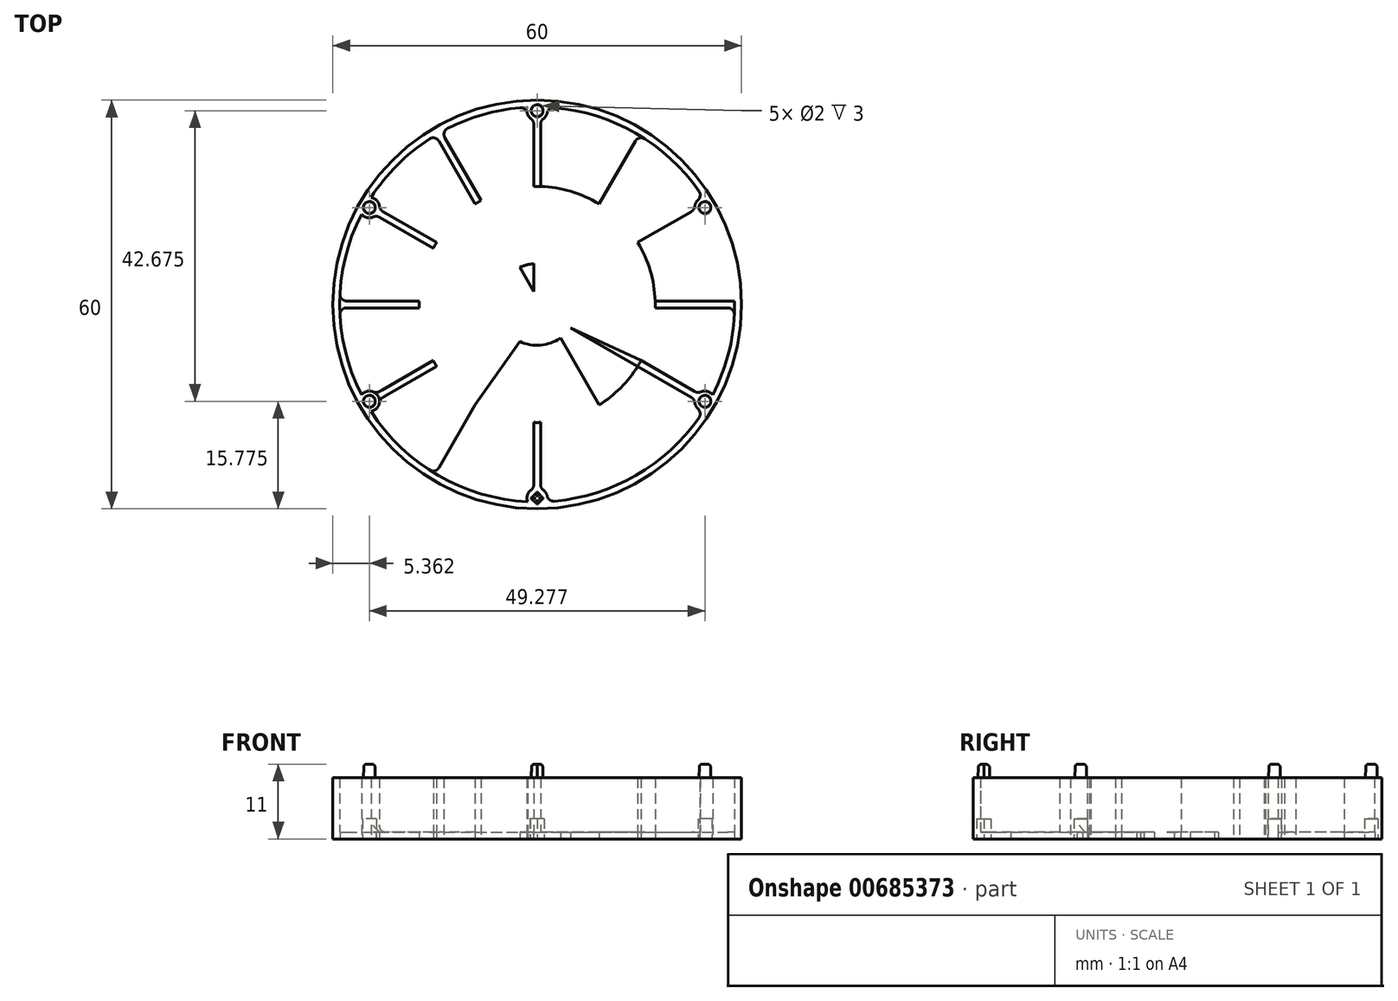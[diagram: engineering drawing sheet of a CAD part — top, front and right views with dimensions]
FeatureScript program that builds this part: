
annotation { "Feature Type Name" : "Feature", "Feature Type Description" : "" }
export const myFeature = defineFeature(function(context is Context, id is Id, definition is map)
    precondition{}
    {
        {
            var Q0;
            Q0=qCreatedBy(makeId("Top.planeOp"),FACE);
            var sketch = newSketch(context, id + "F0", { "sketchPlane" : qUnion([Q0])});
            skCircle(sketch, "E0", {"center": v(0, 0) * mm, "radius": 30 * mm});
            skCircle(sketch, "E1.0", {"center": v(0, 0) * mm, "radius": 29 * mm});
            skLineSegment(sketch, "E2.bottom", {"start": v(14.56, 26.23) * mm, "end": v(15.43, 25.73) * mm});
            skLineSegment(sketch, "E2.top", {"start": v(-15.43, -25.73) * mm, "end": v(-14.56, -26.23) * mm});
            skLineSegment(sketch, "E2.left", {"start": v(14.56, 26.23) * mm, "end": v(-15.43, -25.73) * mm});
            skLineSegment(sketch, "E2.right", {"start": v(15.43, 25.73) * mm, "end": v(-14.56, -26.23) * mm});
            skLineSegment(sketch, "E3.bottom", {"start": v(25.73, 15.43) * mm, "end": v(26.23, 14.56) * mm});
            skLineSegment(sketch, "E3.top", {"start": v(-26.23, -14.56) * mm, "end": v(-25.73, -15.43) * mm});
            skLineSegment(sketch, "E3.left", {"start": v(25.73, 15.43) * mm, "end": v(-26.23, -14.56) * mm});
            skLineSegment(sketch, "E3.right", {"start": v(26.23, 14.56) * mm, "end": v(-25.73, -15.43) * mm});
            skLineSegment(sketch, "E4", {"start": v(-38.35, 0) * mm, "end": v(39.17, 0) * mm, "construction": true});
            skLineSegment(sketch, "E5", {"start": v(0, 42.5) * mm, "end": v(0, -42.47) * mm, "construction": true});
            skLineSegment(sketch, "E6.bottom", {"start": v(-30, 0.5) * mm, "end": v(30, 0.5) * mm});
            skLineSegment(sketch, "E6.top", {"start": v(-30, -0.5) * mm, "end": v(30, -0.5) * mm});
            skLineSegment(sketch, "E6.left", {"start": v(-30, 0.5) * mm, "end": v(-30, -0.5) * mm});
            skLineSegment(sketch, "E6.right", {"start": v(30, 0.5) * mm, "end": v(30, -0.5) * mm});
            skLineSegment(sketch, "E7.bottom", {"start": v(-25.73, 15.43) * mm, "end": v(26.23, -14.56) * mm});
            skLineSegment(sketch, "E7.top", {"start": v(-26.23, 14.56) * mm, "end": v(25.73, -15.43) * mm});
            skLineSegment(sketch, "E7.left", {"start": v(-25.73, 15.43) * mm, "end": v(-26.23, 14.56) * mm});
            skLineSegment(sketch, "E7.right", {"start": v(26.23, -14.56) * mm, "end": v(25.73, -15.43) * mm});
            skLineSegment(sketch, "E8.bottom", {"start": v(-0.5, 30) * mm, "end": v(0.5, 30) * mm});
            skLineSegment(sketch, "E8.top", {"start": v(-0.5, -30) * mm, "end": v(0.5, -30) * mm});
            skLineSegment(sketch, "E8.left", {"start": v(-0.5, 30) * mm, "end": v(-0.5, -30) * mm});
            skLineSegment(sketch, "E8.right", {"start": v(0.5, 30) * mm, "end": v(0.5, -30) * mm});
            skLineSegment(sketch, "E9.bottom", {"start": v(-15.43, 25.73) * mm, "end": v(-14.56, 26.23) * mm});
            skLineSegment(sketch, "E9.top", {"start": v(14.56, -26.23) * mm, "end": v(15.43, -25.73) * mm});
            skLineSegment(sketch, "E9.left", {"start": v(-15.43, 25.73) * mm, "end": v(14.56, -26.23) * mm});
            skLineSegment(sketch, "E9.right", {"start": v(-14.56, 26.23) * mm, "end": v(15.43, -25.73) * mm});
            skCircle(sketch, "E10", {"center": v(0, 0) * mm, "radius": 17.33 * mm});
            skCircle(sketch, "E11", {"center": v(0, 0) * mm, "radius": 6 * mm});
            skLineSegment(sketch, "E12", {"start": v(-9.1, -14.75) * mm, "end": v(-2.56, -5.43) * mm});
            skLineSegment(sketch, "E13", {"start": v(4.93, -3.42) * mm, "end": v(15.25, -8.23) * mm});
            skSolve(sketch);
        }
        {
            var Q0;
            Q0=qCreatedBy(makeId("Top.planeOp"),FACE);
            var sketch = newSketch(context, id + "F1", { "sketchPlane" : qUnion([Q0])});
            skCircle(sketch, "E14", {"center": v(0, 0) * mm, "radius": 30 * mm});
            skCircle(sketch, "E15", {"center": v(0, 0) * mm, "radius": 29 * mm});
            skSolve(sketch);
        }
        {
            var Q0;
            Q0=makeQuery(id+"F1.imprint","IMPRINT",FACE,{"disambiguationData":[TD([[makeQuery(id+"F1.imprint","IMPRINT",EDGE,{"derivedFrom":sQuery(id+"F1.wireOp",EDGE,"E14")}),1.0]])]});
            extrude(context, id + "F2", {"entities" : qUnion([Q0]), "depth" : 9 * mm, "offsetDistance" : 25 * mm});
        }
        {
            var Q0;
            {var subQ0=sQuery(id+"F0.wireOp",EDGE,"E7.bottom");var subQ1=sQuery(id+"F0.wireOp",EDGE,"E1.0");var subQ2=makeQuery(id+"F0.imprint","INTERSECT",VERTEX,{"disambiguationData":[OD(0.0)],"derivedFrom":[subQ1,subQ0]});Q0=makeQuery(id+"F0.imprint","IMPRINT",FACE,{"disambiguationData":[TD([[makeQuery(id+"F0.imprint","IMPRINT",EDGE,{"disambiguationData":[TD([[subQ2,-1.0]])],"derivedFrom":subQ1}),1.0]])]});}
            var Q1;
            {var subQ0=sQuery(id+"F0.wireOp",EDGE,"E8.left");var subQ1=sQuery(id+"F0.wireOp",EDGE,"E1.0");var subQ2=makeQuery(id+"F0.imprint","INTERSECT",VERTEX,{"disambiguationData":[OD(1.0)],"derivedFrom":[subQ1,subQ0]});Q1=makeQuery(id+"F0.imprint","IMPRINT",FACE,{"disambiguationData":[TD([[makeQuery(id+"F0.imprint","IMPRINT",EDGE,{"disambiguationData":[TD([[subQ2,-1.0]])],"derivedFrom":subQ1}),1.0]])]});}
            var Q2;
            {var subQ0=sQuery(id+"F0.wireOp",EDGE,"E9.right");var subQ1=sQuery(id+"F0.wireOp",EDGE,"E1.0");var subQ2=makeQuery(id+"F0.imprint","INTERSECT",VERTEX,{"disambiguationData":[OD(0.0)],"derivedFrom":[subQ1,subQ0]});Q2=makeQuery(id+"F0.imprint","IMPRINT",FACE,{"disambiguationData":[TD([[makeQuery(id+"F0.imprint","IMPRINT",EDGE,{"disambiguationData":[TD([[subQ2,-1.0]])],"derivedFrom":subQ1}),1.0]])]});}
            var Q3;
            {var subQ0=sQuery(id+"F0.wireOp",EDGE,"E8.right");var subQ1=sQuery(id+"F0.wireOp",EDGE,"E1.0");var subQ2=makeQuery(id+"F0.imprint","INTERSECT",VERTEX,{"disambiguationData":[OD(0.0)],"derivedFrom":[subQ1,subQ0]});Q3=makeQuery(id+"F0.imprint","IMPRINT",FACE,{"disambiguationData":[TD([[makeQuery(id+"F0.imprint","IMPRINT",EDGE,{"disambiguationData":[TD([[subQ2,-1.0]])],"derivedFrom":subQ1}),1.0]])]});}
            var Q4;
            {var subQ0=sQuery(id+"F0.wireOp",EDGE,"E3.right");var subQ1=sQuery(id+"F0.wireOp",EDGE,"E1.0");var subQ2=makeQuery(id+"F0.imprint","INTERSECT",VERTEX,{"disambiguationData":[OD(0.0)],"derivedFrom":[subQ1,subQ0]});Q4=makeQuery(id+"F0.imprint","IMPRINT",FACE,{"disambiguationData":[TD([[makeQuery(id+"F0.imprint","IMPRINT",EDGE,{"disambiguationData":[TD([[subQ2,-1.0]])],"derivedFrom":subQ1}),1.0]])]});}
            var Q5;
            {var subQ0=sQuery(id+"F0.wireOp",EDGE,"E7.top");var subQ1=sQuery(id+"F0.wireOp",EDGE,"E1.0");var subQ2=makeQuery(id+"F0.imprint","INTERSECT",VERTEX,{"disambiguationData":[OD(1.0)],"derivedFrom":[subQ1,subQ0]});Q5=makeQuery(id+"F0.imprint","IMPRINT",FACE,{"disambiguationData":[TD([[makeQuery(id+"F0.imprint","IMPRINT",EDGE,{"disambiguationData":[TD([[subQ2,-1.0]])],"derivedFrom":subQ1}),1.0]])]});}
            var Q6;
            {var subQ0=sQuery(id+"F0.wireOp",EDGE,"E6.bottom");var subQ1=sQuery(id+"F0.wireOp",EDGE,"E1.0");var subQ2=makeQuery(id+"F0.imprint","INTERSECT",VERTEX,{"disambiguationData":[OD(1.0)],"derivedFrom":[subQ1,subQ0]});Q6=makeQuery(id+"F0.imprint","IMPRINT",FACE,{"disambiguationData":[TD([[makeQuery(id+"F0.imprint","IMPRINT",EDGE,{"disambiguationData":[TD([[subQ2,-1.0]])],"derivedFrom":subQ1}),1.0]])]});}
            extrude(context, id + "F3", {"entities" : qUnion([Q0, Q1, Q2, Q3, Q4, Q5, Q6]), "operationType" : NewBodyOperationType.ADD, "depth" : 9 * mm, "offsetDistance" : 25 * mm});
        }
        {
            var Q0;
            Q0=makeQuery(id+"F1.imprint","IMPRINT",FACE,{"disambiguationData":[TD([[makeQuery(id+"F1.imprint","IMPRINT",EDGE,{"derivedFrom":sQuery(id+"F1.wireOp",EDGE,"E14")}),1.0]])]});
            var Q1;
            Q1=makeQuery(id+"F1.imprint","IMPRINT",FACE,{"disambiguationData":[TD([[makeQuery(id+"F1.imprint","IMPRINT",EDGE,{"derivedFrom":sQuery(id+"F1.wireOp",EDGE,"E15")}),1.0]])]});
            extrude(context, id + "F4", {"entities" : qUnion([Q0, Q1]), "operationType" : NewBodyOperationType.ADD, "depth" : 1 * mm, "offsetDistance" : 25 * mm});
        }
        {
            var Q0;
            Q0=qCreatedBy(makeId("Top.planeOp"),FACE);
            var sketch = newSketch(context, id + "F5", { "sketchPlane" : qUnion([Q0])});
            skCircle(sketch, "E16", {"center": v(0, 0) * mm, "radius": 28.45 * mm});
            skLineSegment(sketch, "E17", {"start": v(0, 28.45) * mm, "end": v(0, -28.45) * mm, "construction": true});
            skLineSegment(sketch, "E18", {"start": v(24.64, 14.22) * mm, "end": v(0, 0) * mm, "construction": true});
            skLineSegment(sketch, "E19", {"start": v(14.23, 24.64) * mm, "end": v(0, 0) * mm, "construction": true});
            skLineSegment(sketch, "E20", {"start": v(0, 0) * mm, "end": v(28.45, 0) * mm, "construction": true});
            skLineSegment(sketch, "E21", {"start": v(0, 0) * mm, "end": v(24.64, -14.22) * mm, "construction": true});
            skLineSegment(sketch, "E22", {"start": v(0, 0) * mm, "end": v(14.23, -24.64) * mm, "construction": true});
            skLineSegment(sketch, "E23", {"start": v(0, 0) * mm, "end": v(-14.23, 24.64) * mm, "construction": true});
            skLineSegment(sketch, "E24", {"start": v(0, 0) * mm, "end": v(-24.64, 14.22) * mm, "construction": true});
            skLineSegment(sketch, "E25", {"start": v(0, 0) * mm, "end": v(-28.45, 0) * mm, "construction": true});
            skLineSegment(sketch, "E26", {"start": v(0, 0) * mm, "end": v(-24.64, -14.23) * mm, "construction": true});
            skLineSegment(sketch, "E27", {"start": v(0, 0) * mm, "end": v(-14.22, -24.64) * mm, "construction": true});
            skCircle(sketch, "E28", {"center": v(0, 28.45) * mm, "radius": 1.5 * mm});
            skCircle(sketch, "E29", {"center": v(24.64, 14.22) * mm, "radius": 1.5 * mm});
            skCircle(sketch, "E30", {"center": v(24.64, -14.22) * mm, "radius": 1.5 * mm});
            skCircle(sketch, "E31", {"center": v(0, -28.45) * mm, "radius": 1.5 * mm});
            skCircle(sketch, "E32", {"center": v(-24.64, -14.23) * mm, "radius": 1.5 * mm});
            skCircle(sketch, "E33", {"center": v(-24.64, 14.22) * mm, "radius": 1.5 * mm});
            skCircle(sketch, "E34", {"center": v(-24.64, 14.22) * mm, "radius": 1 * mm});
            skCircle(sketch, "E35", {"center": v(0, 28.45) * mm, "radius": 1 * mm});
            skCircle(sketch, "E36", {"center": v(24.64, 14.22) * mm, "radius": 1 * mm});
            skCircle(sketch, "E37", {"center": v(24.64, -14.22) * mm, "radius": 1 * mm});
            skCircle(sketch, "E38", {"center": v(-24.64, -14.23) * mm, "radius": 1 * mm});
            skLineSegment(sketch, "E39.bottom", {"start": v(1.06, -28.45) * mm, "end": v(0, -29.51) * mm});
            skLineSegment(sketch, "E39.top", {"start": v(0, -27.39) * mm, "end": v(-1.06, -28.45) * mm});
            skLineSegment(sketch, "E39.left", {"start": v(1.06, -28.45) * mm, "end": v(0, -27.39) * mm});
            skLineSegment(sketch, "E39.right", {"start": v(0, -29.51) * mm, "end": v(-1.06, -28.45) * mm});
            skSolve(sketch);
        }
        {
            var Q0;
            {var subQ0=sQuery(id+"F0.wireOp",EDGE,"E7.bottom");var subQ1=sQuery(id+"F0.wireOp",EDGE,"E1.0");var subQ2=makeQuery(id+"F0.imprint","INTERSECT",VERTEX,{"disambiguationData":[OD(1.0)],"derivedFrom":[subQ1,subQ0]});Q0=makeQuery(id+"F0.imprint","IMPRINT",FACE,{"disambiguationData":[TD([[makeQuery(id+"F0.imprint","IMPRINT",EDGE,{"disambiguationData":[TD([[subQ2,-1.0]])],"derivedFrom":subQ1}),1.0]])]});}
            var Q1;
            {var subQ0=sQuery(id+"F0.wireOp",EDGE,"E3.left");var subQ1=sQuery(id+"F0.wireOp",EDGE,"E1.0");var subQ2=makeQuery(id+"F0.imprint","INTERSECT",VERTEX,{"disambiguationData":[OD(0.0)],"derivedFrom":[subQ1,subQ0]});Q1=makeQuery(id+"F0.imprint","IMPRINT",FACE,{"disambiguationData":[TD([[makeQuery(id+"F0.imprint","IMPRINT",EDGE,{"disambiguationData":[TD([[subQ2,-1.0]])],"derivedFrom":subQ1}),1.0]])]});}
            var Q2;
            {var subQ0=sQuery(id+"F0.wireOp",EDGE,"E8.left");var subQ1=sQuery(id+"F0.wireOp",EDGE,"E1.0");var subQ2=makeQuery(id+"F0.imprint","INTERSECT",VERTEX,{"disambiguationData":[OD(0.0)],"derivedFrom":[subQ1,subQ0]});Q2=makeQuery(id+"F0.imprint","IMPRINT",FACE,{"disambiguationData":[TD([[makeQuery(id+"F0.imprint","IMPRINT",EDGE,{"disambiguationData":[TD([[subQ2,-1.0]])],"derivedFrom":subQ1}),1.0]])]});}
            var Q3;
            {var subQ0=sQuery(id+"F0.wireOp",EDGE,"E9.left");var subQ1=sQuery(id+"F0.wireOp",EDGE,"E1.0");var subQ2=makeQuery(id+"F0.imprint","INTERSECT",VERTEX,{"disambiguationData":[OD(0.0)],"derivedFrom":[subQ1,subQ0]});Q3=makeQuery(id+"F0.imprint","IMPRINT",FACE,{"disambiguationData":[TD([[makeQuery(id+"F0.imprint","IMPRINT",EDGE,{"disambiguationData":[TD([[subQ2,-1.0]])],"derivedFrom":subQ1}),1.0]])]});}
            var Q4;
            {var subQ0=sQuery(id+"F0.wireOp",EDGE,"E7.top");var subQ1=sQuery(id+"F0.wireOp",EDGE,"E1.0");var subQ2=makeQuery(id+"F0.imprint","INTERSECT",VERTEX,{"disambiguationData":[OD(0.0)],"derivedFrom":[subQ1,subQ0]});Q4=makeQuery(id+"F0.imprint","IMPRINT",FACE,{"disambiguationData":[TD([[makeQuery(id+"F0.imprint","IMPRINT",EDGE,{"disambiguationData":[TD([[subQ2,-1.0]])],"derivedFrom":subQ1}),1.0]])]});}
            var Q5;
            {var subQ0=sQuery(id+"F0.wireOp",EDGE,"E6.top");var subQ1=sQuery(id+"F0.wireOp",EDGE,"E1.0");var subQ2=makeQuery(id+"F0.imprint","INTERSECT",VERTEX,{"disambiguationData":[OD(0.0)],"derivedFrom":[subQ1,subQ0]});Q5=makeQuery(id+"F0.imprint","IMPRINT",FACE,{"disambiguationData":[TD([[makeQuery(id+"F0.imprint","IMPRINT",EDGE,{"disambiguationData":[TD([[subQ2,-1.0]])],"derivedFrom":subQ1}),1.0]])]});}
            var Q6;
            {var subQ0=sQuery(id+"F0.wireOp",EDGE,"E3.right");var subQ1=sQuery(id+"F0.wireOp",EDGE,"E1.0");var subQ2=makeQuery(id+"F0.imprint","INTERSECT",VERTEX,{"disambiguationData":[OD(1.0)],"derivedFrom":[subQ1,subQ0]});Q6=makeQuery(id+"F0.imprint","IMPRINT",FACE,{"disambiguationData":[TD([[makeQuery(id+"F0.imprint","IMPRINT",EDGE,{"disambiguationData":[TD([[subQ2,-1.0]])],"derivedFrom":subQ1}),1.0]])]});}
            extrude(context, id + "F6", {"entities" : qUnion([Q0, Q1, Q2, Q3, Q4, Q5, Q6]), "operationType" : NewBodyOperationType.REMOVE, "depth" : 1 * mm, "offsetDistance" : 25 * mm});
        }
        {
            var Q0;
            {var subQ0=sQuery(id+"F5.wireOp",EDGE,"E33");var subQ1=sQuery(id+"F5.wireOp",EDGE,"E16");var subQ2=makeQuery(id+"F5.imprint","INTERSECT",VERTEX,{"disambiguationData":[OD(0.0)],"derivedFrom":[subQ1,subQ0]});Q0=makeQuery(id+"F5.imprint","IMPRINT",FACE,{"disambiguationData":[TD([[makeQuery(id+"F5.imprint","IMPRINT",EDGE,{"disambiguationData":[TD([[subQ2,-1.0]])],"derivedFrom":subQ1}),1.0]])]});}
            var Q1;
            {var subQ0=sQuery(id+"F5.wireOp",EDGE,"E33");var subQ1=sQuery(id+"F5.wireOp",EDGE,"E16");var subQ2=makeQuery(id+"F5.imprint","INTERSECT",VERTEX,{"disambiguationData":[OD(0.0)],"derivedFrom":[subQ1,subQ0]});Q1=makeQuery(id+"F5.imprint","IMPRINT",FACE,{"disambiguationData":[TD([[makeQuery(id+"F5.imprint","IMPRINT",EDGE,{"disambiguationData":[TD([[subQ2,-1.0]])],"derivedFrom":subQ1}),-1.0]])]});}
            var Q2;
            {var subQ0=sQuery(id+"F5.wireOp",EDGE,"E28");var subQ1=sQuery(id+"F5.wireOp",EDGE,"E16");var subQ2=makeQuery(id+"F5.imprint","INTERSECT",VERTEX,{"disambiguationData":[OD(0.0)],"derivedFrom":[subQ1,subQ0]});Q2=makeQuery(id+"F5.imprint","IMPRINT",FACE,{"disambiguationData":[TD([[makeQuery(id+"F5.imprint","IMPRINT",EDGE,{"disambiguationData":[TD([[subQ2,-1.0]])],"derivedFrom":subQ1}),1.0]])]});}
            var Q3;
            {var subQ0=sQuery(id+"F5.wireOp",EDGE,"E28");var subQ1=sQuery(id+"F5.wireOp",EDGE,"E16");var subQ2=makeQuery(id+"F5.imprint","INTERSECT",VERTEX,{"disambiguationData":[OD(0.0)],"derivedFrom":[subQ1,subQ0]});Q3=makeQuery(id+"F5.imprint","IMPRINT",FACE,{"disambiguationData":[TD([[makeQuery(id+"F5.imprint","IMPRINT",EDGE,{"disambiguationData":[TD([[subQ2,-1.0]])],"derivedFrom":subQ1}),-1.0]])]});}
            var Q4;
            {var subQ0=sQuery(id+"F5.wireOp",EDGE,"E29");var subQ1=sQuery(id+"F5.wireOp",EDGE,"E16");var subQ2=makeQuery(id+"F5.imprint","INTERSECT",VERTEX,{"disambiguationData":[OD(0.0)],"derivedFrom":[subQ1,subQ0]});Q4=makeQuery(id+"F5.imprint","IMPRINT",FACE,{"disambiguationData":[TD([[makeQuery(id+"F5.imprint","IMPRINT",EDGE,{"disambiguationData":[TD([[subQ2,-1.0]])],"derivedFrom":subQ1}),-1.0]])]});}
            var Q5;
            {var subQ0=sQuery(id+"F5.wireOp",EDGE,"E29");var subQ1=sQuery(id+"F5.wireOp",EDGE,"E16");var subQ2=makeQuery(id+"F5.imprint","INTERSECT",VERTEX,{"disambiguationData":[OD(0.0)],"derivedFrom":[subQ1,subQ0]});Q5=makeQuery(id+"F5.imprint","IMPRINT",FACE,{"disambiguationData":[TD([[makeQuery(id+"F5.imprint","IMPRINT",EDGE,{"disambiguationData":[TD([[subQ2,-1.0]])],"derivedFrom":subQ1}),1.0]])]});}
            var Q6;
            {var subQ0=sQuery(id+"F5.wireOp",EDGE,"E32");var subQ1=sQuery(id+"F5.wireOp",EDGE,"E16");var subQ2=makeQuery(id+"F5.imprint","INTERSECT",VERTEX,{"disambiguationData":[OD(0.0)],"derivedFrom":[subQ1,subQ0]});Q6=makeQuery(id+"F5.imprint","IMPRINT",FACE,{"disambiguationData":[TD([[makeQuery(id+"F5.imprint","IMPRINT",EDGE,{"disambiguationData":[TD([[subQ2,-1.0]])],"derivedFrom":subQ1}),1.0]])]});}
            var Q7;
            {var subQ0=sQuery(id+"F5.wireOp",EDGE,"E32");var subQ1=sQuery(id+"F5.wireOp",EDGE,"E16");var subQ2=makeQuery(id+"F5.imprint","INTERSECT",VERTEX,{"disambiguationData":[OD(0.0)],"derivedFrom":[subQ1,subQ0]});Q7=makeQuery(id+"F5.imprint","IMPRINT",FACE,{"disambiguationData":[TD([[makeQuery(id+"F5.imprint","IMPRINT",EDGE,{"disambiguationData":[TD([[subQ2,-1.0]])],"derivedFrom":subQ1}),-1.0]])]});}
            var Q8;
            {var subQ3=sQuery(id+"F5.wireOp",EDGE,"E16");var subQ5=sQuery(id+"F5.wireOp",EDGE,"E31");var subQ6=makeQuery(id+"F5.imprint","INTERSECT",VERTEX,{"disambiguationData":[OD(0.0)],"derivedFrom":[subQ3,subQ5]});Q8=makeQuery(id+"F5.imprint","IMPRINT",FACE,{"disambiguationData":[TD([[makeQuery(id+"F5.imprint","IMPRINT",EDGE,{"disambiguationData":[TD([[subQ6,-1.0]])],"derivedFrom":subQ3}),1.0]])]});}
            var Q9;
            {var subQ6=sQuery(id+"F5.wireOp",EDGE,"E39.bottom");Q9=makeQuery(id+"F5.imprint","IMPRINT",FACE,{"disambiguationData":[TD([[makeQuery(id+"F5.imprint","IMPRINT",EDGE,{"derivedFrom":subQ6}),1.0]])]});}
            var Q10;
            {var subQ0=sQuery(id+"F5.wireOp",EDGE,"E30");var subQ1=sQuery(id+"F5.wireOp",EDGE,"E16");var subQ2=makeQuery(id+"F5.imprint","INTERSECT",VERTEX,{"disambiguationData":[OD(0.0)],"derivedFrom":[subQ1,subQ0]});Q10=makeQuery(id+"F5.imprint","IMPRINT",FACE,{"disambiguationData":[TD([[makeQuery(id+"F5.imprint","IMPRINT",EDGE,{"disambiguationData":[TD([[subQ2,-1.0]])],"derivedFrom":subQ1}),-1.0]])]});}
            var Q11;
            {var subQ0=sQuery(id+"F5.wireOp",EDGE,"E30");var subQ1=sQuery(id+"F5.wireOp",EDGE,"E16");var subQ2=makeQuery(id+"F5.imprint","INTERSECT",VERTEX,{"disambiguationData":[OD(0.0)],"derivedFrom":[subQ1,subQ0]});Q11=makeQuery(id+"F5.imprint","IMPRINT",FACE,{"disambiguationData":[TD([[makeQuery(id+"F5.imprint","IMPRINT",EDGE,{"disambiguationData":[TD([[subQ2,-1.0]])],"derivedFrom":subQ1}),1.0]])]});}
            var Q12;
            {var subQ0=sQuery(id+"F5.wireOp",EDGE,"E34");var subQ1=sQuery(id+"F5.wireOp",EDGE,"E16");var subQ2=makeQuery(id+"F5.imprint","INTERSECT",VERTEX,{"disambiguationData":[OD(0.0)],"derivedFrom":[subQ1,subQ0]});Q12=makeQuery(id+"F5.imprint","IMPRINT",FACE,{"disambiguationData":[TD([[makeQuery(id+"F5.imprint","IMPRINT",EDGE,{"disambiguationData":[TD([[subQ2,-1.0]])],"derivedFrom":subQ1}),1.0]])]});}
            var Q13;
            {var subQ0=sQuery(id+"F5.wireOp",EDGE,"E34");var subQ1=sQuery(id+"F5.wireOp",EDGE,"E16");var subQ2=makeQuery(id+"F5.imprint","INTERSECT",VERTEX,{"disambiguationData":[OD(0.0)],"derivedFrom":[subQ1,subQ0]});Q13=makeQuery(id+"F5.imprint","IMPRINT",FACE,{"disambiguationData":[TD([[makeQuery(id+"F5.imprint","IMPRINT",EDGE,{"disambiguationData":[TD([[subQ2,-1.0]])],"derivedFrom":subQ1}),-1.0]])]});}
            var Q14;
            {var subQ0=sQuery(id+"F5.wireOp",EDGE,"E35");var subQ1=sQuery(id+"F5.wireOp",EDGE,"E16");var subQ2=makeQuery(id+"F5.imprint","INTERSECT",VERTEX,{"disambiguationData":[OD(0.0)],"derivedFrom":[subQ1,subQ0]});Q14=makeQuery(id+"F5.imprint","IMPRINT",FACE,{"disambiguationData":[TD([[makeQuery(id+"F5.imprint","IMPRINT",EDGE,{"disambiguationData":[TD([[subQ2,-1.0]])],"derivedFrom":subQ1}),-1.0]])]});}
            var Q15;
            {var subQ0=sQuery(id+"F5.wireOp",EDGE,"E35");var subQ1=sQuery(id+"F5.wireOp",EDGE,"E16");var subQ2=makeQuery(id+"F5.imprint","INTERSECT",VERTEX,{"disambiguationData":[OD(0.0)],"derivedFrom":[subQ1,subQ0]});Q15=makeQuery(id+"F5.imprint","IMPRINT",FACE,{"disambiguationData":[TD([[makeQuery(id+"F5.imprint","IMPRINT",EDGE,{"disambiguationData":[TD([[subQ2,-1.0]])],"derivedFrom":subQ1}),1.0]])]});}
            var Q16;
            {var subQ0=sQuery(id+"F5.wireOp",EDGE,"E36");var subQ1=sQuery(id+"F5.wireOp",EDGE,"E16");var subQ2=makeQuery(id+"F5.imprint","INTERSECT",VERTEX,{"disambiguationData":[OD(0.0)],"derivedFrom":[subQ1,subQ0]});Q16=makeQuery(id+"F5.imprint","IMPRINT",FACE,{"disambiguationData":[TD([[makeQuery(id+"F5.imprint","IMPRINT",EDGE,{"disambiguationData":[TD([[subQ2,-1.0]])],"derivedFrom":subQ1}),-1.0]])]});}
            var Q17;
            {var subQ0=sQuery(id+"F5.wireOp",EDGE,"E36");var subQ1=sQuery(id+"F5.wireOp",EDGE,"E16");var subQ2=makeQuery(id+"F5.imprint","INTERSECT",VERTEX,{"disambiguationData":[OD(0.0)],"derivedFrom":[subQ1,subQ0]});Q17=makeQuery(id+"F5.imprint","IMPRINT",FACE,{"disambiguationData":[TD([[makeQuery(id+"F5.imprint","IMPRINT",EDGE,{"disambiguationData":[TD([[subQ2,-1.0]])],"derivedFrom":subQ1}),1.0]])]});}
            var Q18;
            {var subQ0=sQuery(id+"F5.wireOp",EDGE,"E37");var subQ1=sQuery(id+"F5.wireOp",EDGE,"E16");var subQ2=makeQuery(id+"F5.imprint","INTERSECT",VERTEX,{"disambiguationData":[OD(0.0)],"derivedFrom":[subQ1,subQ0]});Q18=makeQuery(id+"F5.imprint","IMPRINT",FACE,{"disambiguationData":[TD([[makeQuery(id+"F5.imprint","IMPRINT",EDGE,{"disambiguationData":[TD([[subQ2,-1.0]])],"derivedFrom":subQ1}),-1.0]])]});}
            var Q19;
            {var subQ0=sQuery(id+"F5.wireOp",EDGE,"E37");var subQ1=sQuery(id+"F5.wireOp",EDGE,"E16");var subQ2=makeQuery(id+"F5.imprint","INTERSECT",VERTEX,{"disambiguationData":[OD(0.0)],"derivedFrom":[subQ1,subQ0]});Q19=makeQuery(id+"F5.imprint","IMPRINT",FACE,{"disambiguationData":[TD([[makeQuery(id+"F5.imprint","IMPRINT",EDGE,{"disambiguationData":[TD([[subQ2,-1.0]])],"derivedFrom":subQ1}),1.0]])]});}
            var Q20;
            {var subQ1=sQuery(id+"F5.wireOp",EDGE,"E39.bottom");Q20=makeQuery(id+"F5.imprint","IMPRINT",FACE,{"disambiguationData":[TD([[makeQuery(id+"F5.imprint","IMPRINT",EDGE,{"derivedFrom":subQ1}),-1.0]])]});}
            var Q21;
            {var subQ0=sQuery(id+"F5.wireOp",EDGE,"E38");var subQ1=sQuery(id+"F5.wireOp",EDGE,"E16");var subQ2=makeQuery(id+"F5.imprint","INTERSECT",VERTEX,{"disambiguationData":[OD(0.0)],"derivedFrom":[subQ1,subQ0]});Q21=makeQuery(id+"F5.imprint","IMPRINT",FACE,{"disambiguationData":[TD([[makeQuery(id+"F5.imprint","IMPRINT",EDGE,{"disambiguationData":[TD([[subQ2,-1.0]])],"derivedFrom":subQ1}),-1.0]])]});}
            var Q22;
            {var subQ0=sQuery(id+"F5.wireOp",EDGE,"E38");var subQ1=sQuery(id+"F5.wireOp",EDGE,"E16");var subQ2=makeQuery(id+"F5.imprint","INTERSECT",VERTEX,{"disambiguationData":[OD(0.0)],"derivedFrom":[subQ1,subQ0]});Q22=makeQuery(id+"F5.imprint","IMPRINT",FACE,{"disambiguationData":[TD([[makeQuery(id+"F5.imprint","IMPRINT",EDGE,{"disambiguationData":[TD([[subQ2,-1.0]])],"derivedFrom":subQ1}),1.0]])]});}
            var Q23;
            {var subQ0=sQuery(id+"F5.wireOp",EDGE,"E39.top");var subQ1=sQuery(id+"F5.wireOp",EDGE,"E16");var subQ2=makeQuery(id+"F5.imprint","INTERSECT",VERTEX,{"derivedFrom":[subQ1,subQ0]});Q23=makeQuery(id+"F5.imprint","IMPRINT",FACE,{"disambiguationData":[TD([[makeQuery(id+"F5.imprint","IMPRINT",EDGE,{"disambiguationData":[TD([[subQ2,-1.0]])],"derivedFrom":subQ1}),1.0]])]});}
            extrude(context, id + "F7", {"entities" : qUnion([Q0, Q1, Q2, Q3, Q4, Q5, Q6, Q7, Q8, Q9, Q10, Q11, Q12, Q13, Q14, Q15, Q16, Q17, Q18, Q19, Q20, Q21, Q22, Q23]), "operationType" : NewBodyOperationType.ADD, "depth" : 9 * mm, "offsetDistance" : 25 * mm});
        }
        {
            var Q0;
            {var subQ0=sQuery(id+"F0.wireOp",EDGE,"E8.right");var subQ1=sQuery(id+"F0.wireOp",EDGE,"E1.0");Q0=makeQuery(id+"F3.opExtrude","SWEPT_EDGE",EDGE,{"disambiguationData":[OSD([subQ1,subQ0]),TDD([makeQuery(id+"F0.imprint","INTERSECT",VERTEX,{"disambiguationData":[OD(1.0)],"derivedFrom":[subQ1,subQ0]})])]});}
            var Q1;
            {var subQ0=sQuery(id+"F0.wireOp",EDGE,"E2.left");var subQ1=sQuery(id+"F0.wireOp",EDGE,"E1.0");Q1=makeQuery(id+"F3.opExtrude","SWEPT_EDGE",EDGE,{"disambiguationData":[OSD([subQ1,subQ0]),TDD([makeQuery(id+"F0.imprint","INTERSECT",VERTEX,{"disambiguationData":[OD(1.0)],"derivedFrom":[subQ1,subQ0]})])]});}
            var Q2;
            {var subQ0=sQuery(id+"F0.wireOp",EDGE,"E3.left");var subQ1=sQuery(id+"F0.wireOp",EDGE,"E1.0");Q2=makeQuery(id+"F3.opExtrude","SWEPT_EDGE",EDGE,{"disambiguationData":[OSD([subQ1,subQ0]),TDD([makeQuery(id+"F0.imprint","INTERSECT",VERTEX,{"disambiguationData":[OD(1.0)],"derivedFrom":[subQ1,subQ0]})])]});}
            var Q3;
            {var subQ0=sQuery(id+"F0.wireOp",EDGE,"E6.bottom");var subQ1=sQuery(id+"F0.wireOp",EDGE,"E1.0");Q3=makeQuery(id+"F3.opExtrude","SWEPT_EDGE",EDGE,{"disambiguationData":[OSD([subQ1,subQ0]),TDD([makeQuery(id+"F0.imprint","INTERSECT",VERTEX,{"disambiguationData":[OD(1.0)],"derivedFrom":[subQ1,subQ0]})])]});}
            var Q4;
            {var subQ0=sQuery(id+"F0.wireOp",EDGE,"E9.right");var subQ1=sQuery(id+"F0.wireOp",EDGE,"E1.0");Q4=makeQuery(id+"F3.opExtrude","SWEPT_EDGE",EDGE,{"disambiguationData":[OSD([subQ1,subQ0]),TDD([makeQuery(id+"F0.imprint","INTERSECT",VERTEX,{"disambiguationData":[OD(1.0)],"derivedFrom":[subQ1,subQ0]})])]});}
            var Q5;
            {var subQ0=sQuery(id+"F0.wireOp",EDGE,"E7.bottom");var subQ1=sQuery(id+"F0.wireOp",EDGE,"E1.0");Q5=makeQuery(id+"F3.opExtrude","SWEPT_EDGE",EDGE,{"disambiguationData":[OSD([subQ1,subQ0]),TDD([makeQuery(id+"F0.imprint","INTERSECT",VERTEX,{"disambiguationData":[OD(1.0)],"derivedFrom":[subQ1,subQ0]})])]});}
            var Q6;
            {var subQ0=sQuery(id+"F0.wireOp",EDGE,"E8.left");var subQ1=sQuery(id+"F0.wireOp",EDGE,"E1.0");Q6=makeQuery(id+"F3.opExtrude","SWEPT_EDGE",EDGE,{"disambiguationData":[OSD([subQ1,subQ0]),TDD([makeQuery(id+"F0.imprint","INTERSECT",VERTEX,{"disambiguationData":[OD(0.0)],"derivedFrom":[subQ1,subQ0]})])]});}
            var Q7;
            {var subQ0=sQuery(id+"F0.wireOp",EDGE,"E2.left");var subQ1=sQuery(id+"F0.wireOp",EDGE,"E1.0");Q7=makeQuery(id+"F3.opExtrude","SWEPT_EDGE",EDGE,{"disambiguationData":[OSD([subQ1,subQ0]),TDD([makeQuery(id+"F0.imprint","INTERSECT",VERTEX,{"disambiguationData":[OD(0.0)],"derivedFrom":[subQ1,subQ0]})])]});}
            var Q8;
            {var subQ0=sQuery(id+"F0.wireOp",EDGE,"E3.left");var subQ1=sQuery(id+"F0.wireOp",EDGE,"E1.0");Q8=makeQuery(id+"F3.opExtrude","SWEPT_EDGE",EDGE,{"disambiguationData":[OSD([subQ1,subQ0]),TDD([makeQuery(id+"F0.imprint","INTERSECT",VERTEX,{"disambiguationData":[OD(0.0)],"derivedFrom":[subQ1,subQ0]})])]});}
            var Q9;
            {var subQ0=sQuery(id+"F0.wireOp",EDGE,"E6.top");var subQ1=sQuery(id+"F0.wireOp",EDGE,"E1.0");Q9=makeQuery(id+"F3.opExtrude","SWEPT_EDGE",EDGE,{"disambiguationData":[OSD([subQ1,subQ0]),TDD([makeQuery(id+"F0.imprint","INTERSECT",VERTEX,{"disambiguationData":[OD(1.0)],"derivedFrom":[subQ1,subQ0]})])]});}
            var Q10;
            {var subQ0=sQuery(id+"F0.wireOp",EDGE,"E7.top");var subQ1=sQuery(id+"F0.wireOp",EDGE,"E1.0");Q10=makeQuery(id+"F3.opExtrude","SWEPT_EDGE",EDGE,{"disambiguationData":[OSD([subQ1,subQ0]),TDD([makeQuery(id+"F0.imprint","INTERSECT",VERTEX,{"disambiguationData":[OD(0.0)],"derivedFrom":[subQ1,subQ0]})])]});}
            var Q11;
            {var subQ0=sQuery(id+"F0.wireOp",EDGE,"E6.top");var subQ1=sQuery(id+"F0.wireOp",EDGE,"E1.0");Q11=makeQuery(id+"F3.opExtrude","SWEPT_EDGE",EDGE,{"disambiguationData":[OSD([subQ1,subQ0]),TDD([makeQuery(id+"F0.imprint","INTERSECT",VERTEX,{"disambiguationData":[OD(0.0)],"derivedFrom":[subQ1,subQ0]})])]});}
            var Q12;
            {var subQ0=sQuery(id+"F0.wireOp",EDGE,"E9.left");var subQ1=sQuery(id+"F0.wireOp",EDGE,"E1.0");Q12=makeQuery(id+"F3.opExtrude","SWEPT_EDGE",EDGE,{"disambiguationData":[OSD([subQ1,subQ0]),TDD([makeQuery(id+"F0.imprint","INTERSECT",VERTEX,{"disambiguationData":[OD(0.0)],"derivedFrom":[subQ1,subQ0]})])]});}
            var Q13;
            {var subQ0=sQuery(id+"F0.wireOp",EDGE,"E8.right");var subQ1=sQuery(id+"F0.wireOp",EDGE,"E1.0");Q13=makeQuery(id+"F3.opExtrude","SWEPT_EDGE",EDGE,{"disambiguationData":[OSD([subQ1,subQ0]),TDD([makeQuery(id+"F0.imprint","INTERSECT",VERTEX,{"disambiguationData":[OD(0.0)],"derivedFrom":[subQ1,subQ0]})])]});}
            var Q14;
            {var subQ0=sQuery(id+"F0.wireOp",EDGE,"E7.bottom");var subQ1=sQuery(id+"F0.wireOp",EDGE,"E1.0");Q14=makeQuery(id+"F3.opExtrude","SWEPT_EDGE",EDGE,{"disambiguationData":[OSD([subQ1,subQ0]),TDD([makeQuery(id+"F0.imprint","INTERSECT",VERTEX,{"disambiguationData":[OD(0.0)],"derivedFrom":[subQ1,subQ0]})])]});}
            var Q15;
            {var subQ0=sQuery(id+"F0.wireOp",EDGE,"E9.right");var subQ1=sQuery(id+"F0.wireOp",EDGE,"E1.0");Q15=makeQuery(id+"F3.opExtrude","SWEPT_EDGE",EDGE,{"disambiguationData":[OSD([subQ1,subQ0]),TDD([makeQuery(id+"F0.imprint","INTERSECT",VERTEX,{"disambiguationData":[OD(0.0)],"derivedFrom":[subQ1,subQ0]})])]});}
            var Q16;
            {var subQ0=sQuery(id+"F0.wireOp",EDGE,"E3.right");var subQ1=sQuery(id+"F0.wireOp",EDGE,"E1.0");Q16=makeQuery(id+"F3.opExtrude","SWEPT_EDGE",EDGE,{"disambiguationData":[OSD([subQ1,subQ0]),TDD([makeQuery(id+"F0.imprint","INTERSECT",VERTEX,{"disambiguationData":[OD(1.0)],"derivedFrom":[subQ1,subQ0]})])]});}
            var Q17;
            {var subQ0=sQuery(id+"F0.wireOp",EDGE,"E2.right");var subQ1=sQuery(id+"F0.wireOp",EDGE,"E1.0");Q17=makeQuery(id+"F3.opExtrude","SWEPT_EDGE",EDGE,{"disambiguationData":[OSD([subQ1,subQ0]),TDD([makeQuery(id+"F0.imprint","INTERSECT",VERTEX,{"disambiguationData":[OD(1.0)],"derivedFrom":[subQ1,subQ0]})])]});}
            var Q18;
            {var subQ0=sQuery(id+"F0.wireOp",EDGE,"E3.right");var subQ1=sQuery(id+"F0.wireOp",EDGE,"E1.0");Q18=makeQuery(id+"F3.opExtrude","SWEPT_EDGE",EDGE,{"disambiguationData":[OSD([subQ1,subQ0]),TDD([makeQuery(id+"F0.imprint","INTERSECT",VERTEX,{"disambiguationData":[OD(0.0)],"derivedFrom":[subQ1,subQ0]})])]});}
            var Q19;
            {var subQ0=sQuery(id+"F0.wireOp",EDGE,"E2.right");var subQ1=sQuery(id+"F0.wireOp",EDGE,"E1.0");Q19=makeQuery(id+"F3.opExtrude","SWEPT_EDGE",EDGE,{"disambiguationData":[OSD([subQ1,subQ0]),TDD([makeQuery(id+"F0.imprint","INTERSECT",VERTEX,{"disambiguationData":[OD(0.0)],"derivedFrom":[subQ1,subQ0]})])]});}
            var Q20;
            {var subQ0=sQuery(id+"F0.wireOp",EDGE,"E8.left");var subQ1=sQuery(id+"F0.wireOp",EDGE,"E1.0");Q20=makeQuery(id+"F3.opExtrude","SWEPT_EDGE",EDGE,{"disambiguationData":[OSD([subQ1,subQ0]),TDD([makeQuery(id+"F0.imprint","INTERSECT",VERTEX,{"disambiguationData":[OD(1.0)],"derivedFrom":[subQ1,subQ0]})])]});}
            var Q21;
            {var subQ0=sQuery(id+"F0.wireOp",EDGE,"E9.left");var subQ1=sQuery(id+"F0.wireOp",EDGE,"E1.0");Q21=makeQuery(id+"F3.opExtrude","SWEPT_EDGE",EDGE,{"disambiguationData":[OSD([subQ1,subQ0]),TDD([makeQuery(id+"F0.imprint","INTERSECT",VERTEX,{"disambiguationData":[OD(1.0)],"derivedFrom":[subQ1,subQ0]})])]});}
            var Q22;
            {var subQ0=sQuery(id+"F0.wireOp",EDGE,"E7.top");var subQ1=sQuery(id+"F0.wireOp",EDGE,"E1.0");Q22=makeQuery(id+"F3.opExtrude","SWEPT_EDGE",EDGE,{"disambiguationData":[OSD([subQ1,subQ0]),TDD([makeQuery(id+"F0.imprint","INTERSECT",VERTEX,{"disambiguationData":[OD(1.0)],"derivedFrom":[subQ1,subQ0]})])]});}
            var Q23;
            {var subQ0=sQuery(id+"F0.wireOp",EDGE,"E6.bottom");var subQ1=sQuery(id+"F0.wireOp",EDGE,"E1.0");Q23=makeQuery(id+"F3.opExtrude","SWEPT_EDGE",EDGE,{"disambiguationData":[OSD([subQ1,subQ0]),TDD([makeQuery(id+"F0.imprint","INTERSECT",VERTEX,{"disambiguationData":[OD(0.0)],"derivedFrom":[subQ1,subQ0]})])]});}
            var Q24;
            {var subQ0=sQuery(id+"F0.wireOp",EDGE,"E8.left");var subQ1=sQuery(id+"F0.wireOp",EDGE,"E1.0");var subQ2=makeQuery(id+"F0.imprint","INTERSECT",VERTEX,{"disambiguationData":[OD(0.0)],"derivedFrom":[subQ1,subQ0]});var subQ3=sQuery(id+"F0.wireOp",EDGE,"E9.right");var subQ24=sQuery(id+"F1.wireOp",EDGE,"E15");Q24=makeQuery(id+"F7.boolean.opBoolean","INTERSECT",EDGE,{"derivedFrom":[makeQuery(id+"F6.boolean.opBoolean","MERGE",FACE,{"derivedFrom":[makeQuery(id+"F3.boolean.opBoolean","SPLIT",FACE,{"disambiguationData":[TD([makeQuery(id+"F3.opExtrude","SWEPT_FACE",FACE,{"disambiguationData":[OSD([subQ3])]})])],"derivedFrom":makeQuery(id+"F2.opExtrude","SWEPT_FACE",FACE,{"disambiguationData":[OSD([subQ24])]})}),makeQuery(id+"F6.opExtrude","SWEPT_FACE",FACE,{"disambiguationData":[OSD([subQ1]),TDD([makeQuery(id+"F0.imprint","IMPRINT",EDGE,{"disambiguationData":[TD([[subQ2,-1.0]])],"derivedFrom":subQ1})])]})]}),makeQuery(id+"F7.opExtrude","SWEPT_FACE",FACE,{"disambiguationData":[OSD([sQuery(id+"F5.wireOp",EDGE,"E28")])]})]});}
            var Q25;
            {var subQ0=sQuery(id+"F0.wireOp",EDGE,"E7.bottom");var subQ1=sQuery(id+"F0.wireOp",EDGE,"E1.0");var subQ2=makeQuery(id+"F0.imprint","INTERSECT",VERTEX,{"disambiguationData":[OD(1.0)],"derivedFrom":[subQ1,subQ0]});var subQ26=sQuery(id+"F1.wireOp",EDGE,"E15");var subQ36=sQuery(id+"F0.wireOp",EDGE,"E3.right");Q25=makeQuery(id+"F7.boolean.opBoolean","INTERSECT",EDGE,{"derivedFrom":[makeQuery(id+"F6.boolean.opBoolean","MERGE",FACE,{"derivedFrom":[makeQuery(id+"F3.boolean.opBoolean","SPLIT",FACE,{"disambiguationData":[TD([makeQuery(id+"F3.opExtrude","SWEPT_FACE",FACE,{"disambiguationData":[OSD([subQ36])]})])],"derivedFrom":makeQuery(id+"F2.opExtrude","SWEPT_FACE",FACE,{"disambiguationData":[OSD([subQ26])]})}),makeQuery(id+"F6.opExtrude","SWEPT_FACE",FACE,{"disambiguationData":[OSD([subQ1]),TDD([makeQuery(id+"F0.imprint","IMPRINT",EDGE,{"disambiguationData":[TD([[subQ2,-1.0]])],"derivedFrom":subQ1})])]})]}),makeQuery(id+"F7.opExtrude","SWEPT_FACE",FACE,{"disambiguationData":[OSD([sQuery(id+"F5.wireOp",EDGE,"E29")])]})]});}
            var Q26;
            Q26=makeQuery(id+"F7.boolean.opBoolean","INTERSECT",EDGE,{"derivedFrom":[makeQuery(id+"F3.opExtrude","SWEPT_FACE",FACE,{"disambiguationData":[OSD([sQuery(id+"F0.wireOp",EDGE,"E3.right")])]}),makeQuery(id+"F7.opExtrude","SWEPT_FACE",FACE,{"disambiguationData":[OSD([sQuery(id+"F5.wireOp",EDGE,"E29")])]})]});
            var Q27;
            {var subQ0=sQuery(id+"F0.wireOp",EDGE,"E8.left");Q27=makeQuery(id+"F7.boolean.opBoolean","INTERSECT",EDGE,{"derivedFrom":[makeQuery(id+"F6.boolean.opBoolean","MERGE",FACE,{"derivedFrom":[makeQuery(id+"F3.opExtrude","SWEPT_FACE",FACE,{"disambiguationData":[OSD([subQ0]),TDD([makeQuery(id+"F0.imprint","IMPRINT",EDGE,{"disambiguationData":[TD([[makeQuery(id+"F0.imprint","INTERSECT",VERTEX,{"disambiguationData":[OD(0.0)],"derivedFrom":[sQuery(id+"F0.wireOp",EDGE,"E1.0"),subQ0]}),-1.0]])],"derivedFrom":subQ0})])]}),makeQuery(id+"F6.opExtrude","SWEPT_FACE",FACE,{"disambiguationData":[OSD([subQ0])]})]}),makeQuery(id+"F7.opExtrude","SWEPT_FACE",FACE,{"disambiguationData":[OSD([sQuery(id+"F5.wireOp",EDGE,"E28")])]})]});}
            var Q28;
            {var subQ0=sQuery(id+"F0.wireOp",EDGE,"E3.left");var subQ1=sQuery(id+"F0.wireOp",EDGE,"E1.0");var subQ25=sQuery(id+"F1.wireOp",EDGE,"E15");Q28=makeQuery(id+"F7.boolean.opBoolean","INTERSECT",EDGE,{"derivedFrom":[makeQuery(id+"F6.boolean.opBoolean","MERGE",FACE,{"derivedFrom":[makeQuery(id+"F3.boolean.opBoolean","SPLIT",FACE,{"disambiguationData":[TD([makeQuery(id+"F3.opExtrude","SWEPT_FACE",FACE,{"disambiguationData":[OSD([subQ0])]})])],"derivedFrom":makeQuery(id+"F2.opExtrude","SWEPT_FACE",FACE,{"disambiguationData":[OSD([subQ25])]})}),makeQuery(id+"F6.opExtrude","SWEPT_FACE",FACE,{"disambiguationData":[OSD([subQ1]),TDD([makeQuery(id+"F0.imprint","IMPRINT",EDGE,{"disambiguationData":[TD([[makeQuery(id+"F0.imprint","INTERSECT",VERTEX,{"disambiguationData":[OD(0.0)],"derivedFrom":[subQ1,subQ0]}),-1.0]])],"derivedFrom":subQ1})])]})]}),makeQuery(id+"F7.opExtrude","SWEPT_FACE",FACE,{"disambiguationData":[OSD([sQuery(id+"F5.wireOp",EDGE,"E28")])]})]});}
            var Q29;
            {var subQ0=sQuery(id+"F0.wireOp",EDGE,"E8.right");Q29=makeQuery(id+"F7.boolean.opBoolean","INTERSECT",EDGE,{"derivedFrom":[makeQuery(id+"F3.opExtrude","SWEPT_FACE",FACE,{"disambiguationData":[OSD([subQ0]),TDD([makeQuery(id+"F0.imprint","IMPRINT",EDGE,{"disambiguationData":[TD([[makeQuery(id+"F0.imprint","INTERSECT",VERTEX,{"disambiguationData":[OD(0.0)],"derivedFrom":[sQuery(id+"F0.wireOp",EDGE,"E1.0"),subQ0]}),-1.0]])],"derivedFrom":subQ0})])]}),makeQuery(id+"F7.opExtrude","SWEPT_FACE",FACE,{"disambiguationData":[OSD([sQuery(id+"F5.wireOp",EDGE,"E28")])]})]});}
            var Q30;
            {var subQ0=sQuery(id+"F0.wireOp",EDGE,"E7.top");var subQ1=sQuery(id+"F0.wireOp",EDGE,"E1.0");var subQ2=makeQuery(id+"F0.imprint","INTERSECT",VERTEX,{"disambiguationData":[OD(0.0)],"derivedFrom":[subQ1,subQ0]});var subQ3=sQuery(id+"F0.wireOp",EDGE,"E6.bottom");var subQ25=sQuery(id+"F1.wireOp",EDGE,"E15");Q30=makeQuery(id+"F7.boolean.opBoolean","INTERSECT",EDGE,{"derivedFrom":[makeQuery(id+"F6.boolean.opBoolean","MERGE",FACE,{"derivedFrom":[makeQuery(id+"F3.boolean.opBoolean","SPLIT",FACE,{"disambiguationData":[TD([makeQuery(id+"F3.opExtrude","SWEPT_FACE",FACE,{"disambiguationData":[OSD([subQ3])]})])],"derivedFrom":makeQuery(id+"F2.opExtrude","SWEPT_FACE",FACE,{"disambiguationData":[OSD([subQ25])]})}),makeQuery(id+"F6.opExtrude","SWEPT_FACE",FACE,{"disambiguationData":[OSD([subQ1]),TDD([makeQuery(id+"F0.imprint","IMPRINT",EDGE,{"disambiguationData":[TD([[subQ2,-1.0]])],"derivedFrom":subQ1})])]})]}),makeQuery(id+"F7.opExtrude","SWEPT_FACE",FACE,{"disambiguationData":[OSD([sQuery(id+"F5.wireOp",EDGE,"E33")])]})]});}
            var Q31;
            {var subQ0=sQuery(id+"F0.wireOp",EDGE,"E3.right");var subQ1=sQuery(id+"F0.wireOp",EDGE,"E1.0");var subQ2=sQuery(id+"F0.wireOp",EDGE,"E6.top");var subQ30=sQuery(id+"F1.wireOp",EDGE,"E15");Q31=makeQuery(id+"F7.boolean.opBoolean","INTERSECT",EDGE,{"disambiguationData":[OD(1.0)],"derivedFrom":[makeQuery(id+"F6.boolean.opBoolean","MERGE",FACE,{"derivedFrom":[makeQuery(id+"F3.boolean.opBoolean","SPLIT",FACE,{"disambiguationData":[TD([makeQuery(id+"F3.opExtrude","SWEPT_FACE",FACE,{"disambiguationData":[OSD([subQ2])]})])],"derivedFrom":makeQuery(id+"F2.opExtrude","SWEPT_FACE",FACE,{"disambiguationData":[OSD([subQ30])]})}),makeQuery(id+"F6.opExtrude","SWEPT_FACE",FACE,{"disambiguationData":[OSD([subQ1]),TDD([makeQuery(id+"F0.imprint","IMPRINT",EDGE,{"disambiguationData":[TD([[makeQuery(id+"F0.imprint","INTERSECT",VERTEX,{"disambiguationData":[OD(0.0)],"derivedFrom":[subQ1,subQ2]}),-1.0]])],"derivedFrom":subQ1})])]}),makeQuery(id+"F6.opExtrude","SWEPT_FACE",FACE,{"disambiguationData":[OSD([subQ1]),TDD([makeQuery(id+"F0.imprint","IMPRINT",EDGE,{"disambiguationData":[TD([[makeQuery(id+"F0.imprint","INTERSECT",VERTEX,{"disambiguationData":[OD(1.0)],"derivedFrom":[subQ1,subQ0]}),-1.0]])],"derivedFrom":subQ1})])]})]}),makeQuery(id+"F7.opExtrude","SWEPT_FACE",FACE,{"disambiguationData":[OSD([sQuery(id+"F5.wireOp",EDGE,"E32")])]})]});}
            var Q32;
            {var subQ0=sQuery(id+"F0.wireOp",EDGE,"E3.right");var subQ1=sQuery(id+"F0.wireOp",EDGE,"E1.0");var subQ2=sQuery(id+"F0.wireOp",EDGE,"E6.top");var subQ30=sQuery(id+"F1.wireOp",EDGE,"E15");Q32=makeQuery(id+"F7.boolean.opBoolean","INTERSECT",EDGE,{"disambiguationData":[OD(0.0)],"derivedFrom":[makeQuery(id+"F6.boolean.opBoolean","MERGE",FACE,{"derivedFrom":[makeQuery(id+"F3.boolean.opBoolean","SPLIT",FACE,{"disambiguationData":[TD([makeQuery(id+"F3.opExtrude","SWEPT_FACE",FACE,{"disambiguationData":[OSD([subQ2])]})])],"derivedFrom":makeQuery(id+"F2.opExtrude","SWEPT_FACE",FACE,{"disambiguationData":[OSD([subQ30])]})}),makeQuery(id+"F6.opExtrude","SWEPT_FACE",FACE,{"disambiguationData":[OSD([subQ1]),TDD([makeQuery(id+"F0.imprint","IMPRINT",EDGE,{"disambiguationData":[TD([[makeQuery(id+"F0.imprint","INTERSECT",VERTEX,{"disambiguationData":[OD(0.0)],"derivedFrom":[subQ1,subQ2]}),-1.0]])],"derivedFrom":subQ1})])]}),makeQuery(id+"F6.opExtrude","SWEPT_FACE",FACE,{"disambiguationData":[OSD([subQ1]),TDD([makeQuery(id+"F0.imprint","IMPRINT",EDGE,{"disambiguationData":[TD([[makeQuery(id+"F0.imprint","INTERSECT",VERTEX,{"disambiguationData":[OD(1.0)],"derivedFrom":[subQ1,subQ0]}),-1.0]])],"derivedFrom":subQ1})])]})]}),makeQuery(id+"F7.opExtrude","SWEPT_FACE",FACE,{"disambiguationData":[OSD([sQuery(id+"F5.wireOp",EDGE,"E32")])]})]});}
            var Q33;
            {var subQ3=sQuery(id+"F0.wireOp",EDGE,"E7.top");var subQ6=sQuery(id+"F0.wireOp",EDGE,"E1.0");var subQ24=makeQuery(id+"F0.imprint","INTERSECT",VERTEX,{"disambiguationData":[OD(1.0)],"derivedFrom":[subQ6,subQ3]});var subQ26=makeQuery(id+"F0.imprint","IMPRINT",EDGE,{"disambiguationData":[TD([[subQ24,1.0]])],"derivedFrom":subQ3});var subQ27=sQuery(id+"F1.wireOp",EDGE,"E15");Q33=makeQuery(id+"F7.boolean.opBoolean","INTERSECT",EDGE,{"derivedFrom":[makeQuery(id+"F3.boolean.opBoolean","SPLIT",FACE,{"disambiguationData":[TD([makeQuery(id+"F3.opExtrude","SWEPT_FACE",FACE,{"disambiguationData":[OSD([subQ3]),TDD([subQ26])]})])],"derivedFrom":makeQuery(id+"F2.opExtrude","SWEPT_FACE",FACE,{"disambiguationData":[OSD([subQ27])]})}),makeQuery(id+"F7.opExtrude","SWEPT_FACE",FACE,{"disambiguationData":[OSD([sQuery(id+"F5.wireOp",EDGE,"E31")])]})]});}
            var Q34;
            {var subQ0=sQuery(id+"F0.wireOp",EDGE,"E7.bottom");var subQ1=sQuery(id+"F0.wireOp",EDGE,"E1.0");var subQ2=makeQuery(id+"F0.imprint","INTERSECT",VERTEX,{"disambiguationData":[OD(1.0)],"derivedFrom":[subQ1,subQ0]});var subQ26=sQuery(id+"F1.wireOp",EDGE,"E15");var subQ36=sQuery(id+"F0.wireOp",EDGE,"E3.right");Q34=makeQuery(id+"F7.boolean.opBoolean","INTERSECT",EDGE,{"derivedFrom":[makeQuery(id+"F6.boolean.opBoolean","MERGE",FACE,{"derivedFrom":[makeQuery(id+"F3.boolean.opBoolean","SPLIT",FACE,{"disambiguationData":[TD([makeQuery(id+"F3.opExtrude","SWEPT_FACE",FACE,{"disambiguationData":[OSD([subQ36])]})])],"derivedFrom":makeQuery(id+"F2.opExtrude","SWEPT_FACE",FACE,{"disambiguationData":[OSD([subQ26])]})}),makeQuery(id+"F6.opExtrude","SWEPT_FACE",FACE,{"disambiguationData":[OSD([subQ1]),TDD([makeQuery(id+"F0.imprint","IMPRINT",EDGE,{"disambiguationData":[TD([[subQ2,-1.0]])],"derivedFrom":subQ1})])]})]}),makeQuery(id+"F7.opExtrude","SWEPT_FACE",FACE,{"disambiguationData":[OSD([sQuery(id+"F5.wireOp",EDGE,"E30")])]})]});}
            var Q35;
            {var subQ0=sQuery(id+"F0.wireOp",EDGE,"E3.right");var subQ1=sQuery(id+"F0.wireOp",EDGE,"E1.0");var subQ2=sQuery(id+"F0.wireOp",EDGE,"E6.top");var subQ30=sQuery(id+"F1.wireOp",EDGE,"E15");Q35=makeQuery(id+"F7.boolean.opBoolean","INTERSECT",EDGE,{"derivedFrom":[makeQuery(id+"F6.boolean.opBoolean","MERGE",FACE,{"derivedFrom":[makeQuery(id+"F3.boolean.opBoolean","SPLIT",FACE,{"disambiguationData":[TD([makeQuery(id+"F3.opExtrude","SWEPT_FACE",FACE,{"disambiguationData":[OSD([subQ2])]})])],"derivedFrom":makeQuery(id+"F2.opExtrude","SWEPT_FACE",FACE,{"disambiguationData":[OSD([subQ30])]})}),makeQuery(id+"F6.opExtrude","SWEPT_FACE",FACE,{"disambiguationData":[OSD([subQ1]),TDD([makeQuery(id+"F0.imprint","IMPRINT",EDGE,{"disambiguationData":[TD([[makeQuery(id+"F0.imprint","INTERSECT",VERTEX,{"disambiguationData":[OD(0.0)],"derivedFrom":[subQ1,subQ2]}),-1.0]])],"derivedFrom":subQ1})])]}),makeQuery(id+"F6.opExtrude","SWEPT_FACE",FACE,{"disambiguationData":[OSD([subQ1]),TDD([makeQuery(id+"F0.imprint","IMPRINT",EDGE,{"disambiguationData":[TD([[makeQuery(id+"F0.imprint","INTERSECT",VERTEX,{"disambiguationData":[OD(1.0)],"derivedFrom":[subQ1,subQ0]}),-1.0]])],"derivedFrom":subQ1})])]})]}),makeQuery(id+"F7.opExtrude","SWEPT_FACE",FACE,{"disambiguationData":[OSD([sQuery(id+"F5.wireOp",EDGE,"E31")])]})]});}
            var Q36;
            {var subQ3=sQuery(id+"F0.wireOp",EDGE,"E7.top");var subQ6=sQuery(id+"F0.wireOp",EDGE,"E1.0");var subQ24=makeQuery(id+"F0.imprint","INTERSECT",VERTEX,{"disambiguationData":[OD(1.0)],"derivedFrom":[subQ6,subQ3]});var subQ26=makeQuery(id+"F0.imprint","IMPRINT",EDGE,{"disambiguationData":[TD([[subQ24,1.0]])],"derivedFrom":subQ3});var subQ27=sQuery(id+"F1.wireOp",EDGE,"E15");Q36=makeQuery(id+"F7.boolean.opBoolean","INTERSECT",EDGE,{"derivedFrom":[makeQuery(id+"F3.boolean.opBoolean","SPLIT",FACE,{"disambiguationData":[TD([makeQuery(id+"F3.opExtrude","SWEPT_FACE",FACE,{"disambiguationData":[OSD([subQ3]),TDD([subQ26])]})])],"derivedFrom":makeQuery(id+"F2.opExtrude","SWEPT_FACE",FACE,{"disambiguationData":[OSD([subQ27])]})}),makeQuery(id+"F7.opExtrude","SWEPT_FACE",FACE,{"disambiguationData":[OSD([sQuery(id+"F5.wireOp",EDGE,"E30")])]})]});}
            var Q37;
            {var subQ0=sQuery(id+"F0.wireOp",EDGE,"E3.left");var subQ1=sQuery(id+"F0.wireOp",EDGE,"E1.0");var subQ25=sQuery(id+"F1.wireOp",EDGE,"E15");Q37=makeQuery(id+"F7.boolean.opBoolean","INTERSECT",EDGE,{"derivedFrom":[makeQuery(id+"F6.boolean.opBoolean","MERGE",FACE,{"derivedFrom":[makeQuery(id+"F3.boolean.opBoolean","SPLIT",FACE,{"disambiguationData":[TD([makeQuery(id+"F3.opExtrude","SWEPT_FACE",FACE,{"disambiguationData":[OSD([subQ0])]})])],"derivedFrom":makeQuery(id+"F2.opExtrude","SWEPT_FACE",FACE,{"disambiguationData":[OSD([subQ25])]})}),makeQuery(id+"F6.opExtrude","SWEPT_FACE",FACE,{"disambiguationData":[OSD([subQ1]),TDD([makeQuery(id+"F0.imprint","IMPRINT",EDGE,{"disambiguationData":[TD([[makeQuery(id+"F0.imprint","INTERSECT",VERTEX,{"disambiguationData":[OD(0.0)],"derivedFrom":[subQ1,subQ0]}),-1.0]])],"derivedFrom":subQ1})])]})]}),makeQuery(id+"F7.opExtrude","SWEPT_FACE",FACE,{"disambiguationData":[OSD([sQuery(id+"F5.wireOp",EDGE,"E29")])]})]});}
            var Q38;
            {var subQ0=sQuery(id+"F0.wireOp",EDGE,"E8.right");Q38=makeQuery(id+"F7.boolean.opBoolean","INTERSECT",EDGE,{"derivedFrom":[makeQuery(id+"F3.opExtrude","SWEPT_FACE",FACE,{"disambiguationData":[OSD([subQ0]),TDD([makeQuery(id+"F0.imprint","IMPRINT",EDGE,{"disambiguationData":[TD([[makeQuery(id+"F0.imprint","INTERSECT",VERTEX,{"disambiguationData":[OD(1.0)],"derivedFrom":[sQuery(id+"F0.wireOp",EDGE,"E1.0"),subQ0]}),1.0]])],"derivedFrom":subQ0})])]}),makeQuery(id+"F7.opExtrude","SWEPT_FACE",FACE,{"disambiguationData":[OSD([sQuery(id+"F5.wireOp",EDGE,"E31")])]})]});}
            var Q39;
            {var subQ0=sQuery(id+"F0.wireOp",EDGE,"E8.left");Q39=makeQuery(id+"F7.boolean.opBoolean","INTERSECT",EDGE,{"derivedFrom":[makeQuery(id+"F3.opExtrude","SWEPT_FACE",FACE,{"disambiguationData":[OSD([subQ0]),TDD([makeQuery(id+"F0.imprint","IMPRINT",EDGE,{"disambiguationData":[TD([[makeQuery(id+"F0.imprint","INTERSECT",VERTEX,{"disambiguationData":[OD(1.0)],"derivedFrom":[sQuery(id+"F0.wireOp",EDGE,"E1.0"),subQ0]}),1.0]])],"derivedFrom":subQ0})])]}),makeQuery(id+"F7.opExtrude","SWEPT_FACE",FACE,{"disambiguationData":[OSD([sQuery(id+"F5.wireOp",EDGE,"E31")])]})]});}
            var Q40;
            {var subQ0=sQuery(id+"F0.wireOp",EDGE,"E3.left");Q40=makeQuery(id+"F7.boolean.opBoolean","INTERSECT",EDGE,{"derivedFrom":[makeQuery(id+"F6.boolean.opBoolean","COPY",FACE,{"derivedFrom":makeQuery(id+"F6.opExtrude","SWEPT_FACE",FACE,{"disambiguationData":[OSD([subQ0]),TDD([makeQuery(id+"F0.imprint","IMPRINT",EDGE,{"disambiguationData":[TD([[makeQuery(id+"F0.imprint","INTERSECT",VERTEX,{"disambiguationData":[OD(1.0)],"derivedFrom":[sQuery(id+"F0.wireOp",EDGE,"E1.0"),subQ0]}),1.0]])],"derivedFrom":subQ0})])]})}),makeQuery(id+"F7.opExtrude","SWEPT_FACE",FACE,{"disambiguationData":[OSD([sQuery(id+"F5.wireOp",EDGE,"E32")])]})]});}
            var Q41;
            Q41=makeQuery(id+"F7.boolean.opBoolean","INTERSECT",EDGE,{"derivedFrom":[makeQuery(id+"F6.boolean.opBoolean","COPY",FACE,{"derivedFrom":makeQuery(id+"F6.opExtrude","SWEPT_FACE",FACE,{"disambiguationData":[OSD([sQuery(id+"F0.wireOp",EDGE,"E3.right")])]})}),makeQuery(id+"F7.opExtrude","SWEPT_FACE",FACE,{"disambiguationData":[OSD([sQuery(id+"F5.wireOp",EDGE,"E32")])]})]});
            var Q42;
            {var subQ0=sQuery(id+"F0.wireOp",EDGE,"E7.top");Q42=makeQuery(id+"F7.boolean.opBoolean","INTERSECT",EDGE,{"derivedFrom":[makeQuery(id+"F6.boolean.opBoolean","MERGE",FACE,{"derivedFrom":[makeQuery(id+"F3.opExtrude","SWEPT_FACE",FACE,{"disambiguationData":[OSD([subQ0]),TDD([makeQuery(id+"F0.imprint","IMPRINT",EDGE,{"disambiguationData":[TD([[makeQuery(id+"F0.imprint","INTERSECT",VERTEX,{"disambiguationData":[OD(0.0)],"derivedFrom":[sQuery(id+"F0.wireOp",EDGE,"E1.0"),subQ0]}),-1.0]])],"derivedFrom":subQ0})])]}),makeQuery(id+"F6.opExtrude","SWEPT_FACE",FACE,{"disambiguationData":[OSD([subQ0])]})]}),makeQuery(id+"F7.opExtrude","SWEPT_FACE",FACE,{"disambiguationData":[OSD([sQuery(id+"F5.wireOp",EDGE,"E33")])]})]});}
            var Q43;
            {var subQ0=sQuery(id+"F0.wireOp",EDGE,"E7.bottom");var subQ1=makeQuery(id+"F0.imprint","IMPRINT",EDGE,{"disambiguationData":[TD([[makeQuery(id+"F0.imprint","INTERSECT",VERTEX,{"disambiguationData":[OD(0.0)],"derivedFrom":[sQuery(id+"F0.wireOp",EDGE,"E1.0"),subQ0]}),-1.0]])],"derivedFrom":subQ0});Q43=makeQuery(id+"F7.boolean.opBoolean","INTERSECT",EDGE,{"derivedFrom":[makeQuery(id+"F6.boolean.opBoolean","MERGE",FACE,{"derivedFrom":[makeQuery(id+"F3.opExtrude","SWEPT_FACE",FACE,{"disambiguationData":[OSD([subQ0]),TDD([subQ1])]}),makeQuery(id+"F6.opExtrude","SWEPT_FACE",FACE,{"disambiguationData":[OSD([subQ0]),TDD([subQ1])]})]}),makeQuery(id+"F7.opExtrude","SWEPT_FACE",FACE,{"disambiguationData":[OSD([sQuery(id+"F5.wireOp",EDGE,"E33")])]})]});}
            var Q44;
            {var subQ0=sQuery(id+"F0.wireOp",EDGE,"E7.top");Q44=makeQuery(id+"F7.boolean.opBoolean","INTERSECT",EDGE,{"derivedFrom":[makeQuery(id+"F3.opExtrude","SWEPT_FACE",FACE,{"disambiguationData":[OSD([subQ0]),TDD([makeQuery(id+"F0.imprint","IMPRINT",EDGE,{"disambiguationData":[TD([[makeQuery(id+"F0.imprint","INTERSECT",VERTEX,{"disambiguationData":[OD(1.0)],"derivedFrom":[sQuery(id+"F0.wireOp",EDGE,"E1.0"),subQ0]}),1.0]])],"derivedFrom":subQ0})])]}),makeQuery(id+"F7.opExtrude","SWEPT_FACE",FACE,{"disambiguationData":[OSD([sQuery(id+"F5.wireOp",EDGE,"E30")])]})]});}
            var Q45;
            {var subQ0=sQuery(id+"F0.wireOp",EDGE,"E7.bottom");var subQ1=makeQuery(id+"F0.imprint","IMPRINT",EDGE,{"disambiguationData":[TD([[makeQuery(id+"F0.imprint","INTERSECT",VERTEX,{"disambiguationData":[OD(1.0)],"derivedFrom":[sQuery(id+"F0.wireOp",EDGE,"E1.0"),subQ0]}),1.0]])],"derivedFrom":subQ0});Q45=makeQuery(id+"F7.boolean.opBoolean","INTERSECT",EDGE,{"derivedFrom":[makeQuery(id+"F6.boolean.opBoolean","MERGE",FACE,{"derivedFrom":[makeQuery(id+"F3.opExtrude","SWEPT_FACE",FACE,{"disambiguationData":[OSD([subQ0]),TDD([subQ1])]}),makeQuery(id+"F6.opExtrude","SWEPT_FACE",FACE,{"disambiguationData":[OSD([subQ0]),TDD([subQ1])]})]}),makeQuery(id+"F7.opExtrude","SWEPT_FACE",FACE,{"disambiguationData":[OSD([sQuery(id+"F5.wireOp",EDGE,"E30")])]})]});}
            var Q46;
            {var subQ0=sQuery(id+"F0.wireOp",EDGE,"E3.left");Q46=makeQuery(id+"F7.boolean.opBoolean","INTERSECT",EDGE,{"derivedFrom":[makeQuery(id+"F6.boolean.opBoolean","MERGE",FACE,{"derivedFrom":[makeQuery(id+"F3.opExtrude","SWEPT_FACE",FACE,{"disambiguationData":[OSD([subQ0])]}),makeQuery(id+"F6.opExtrude","SWEPT_FACE",FACE,{"disambiguationData":[OSD([subQ0]),TDD([makeQuery(id+"F0.imprint","IMPRINT",EDGE,{"disambiguationData":[TD([[makeQuery(id+"F0.imprint","INTERSECT",VERTEX,{"disambiguationData":[OD(0.0)],"derivedFrom":[sQuery(id+"F0.wireOp",EDGE,"E1.0"),subQ0]}),-1.0]])],"derivedFrom":subQ0})])]})]}),makeQuery(id+"F7.opExtrude","SWEPT_FACE",FACE,{"disambiguationData":[OSD([sQuery(id+"F5.wireOp",EDGE,"E29")])]})]});}
            var Q47;
            Q47=makeQuery(id+"F7.boolean.opBoolean","INTERSECT",EDGE,{"derivedFrom":[makeQuery(id+"F4.opExtrude","CAP_FACE",FACE,{"disambiguationData":[OSD([sQuery(id+"F1.wireOp",EDGE,"E14")])],"isStart":false}),makeQuery(id+"F7.opExtrude","SWEPT_FACE",FACE,{"disambiguationData":[OSD([sQuery(id+"F5.wireOp",EDGE,"E32")])]})]});
            fillet(context, id + "F8", {"entities" : qUnion([Q0, Q1, Q2, Q3, Q4, Q5, Q6, Q7, Q8, Q9, Q10, Q11, Q12, Q13, Q14, Q15, Q16, Q17, Q18, Q19, Q20, Q21, Q22, Q23, Q24, Q25, Q26, Q27, Q28, Q29, Q30, Q31, Q32, Q33, Q34, Q35, Q36, Q37, Q38, Q39, Q40, Q41, Q42, Q43, Q44, Q45, Q46, Q47]), "radius" : 1 * mm, "tangentPropagation" : true, "allowEdgeOverflow" : false});
        }
        {
            var Q0;
            {var subQ0=sQuery(id+"F5.wireOp",EDGE,"E34");var subQ1=sQuery(id+"F5.wireOp",EDGE,"E16");var subQ2=makeQuery(id+"F5.imprint","INTERSECT",VERTEX,{"disambiguationData":[OD(0.0)],"derivedFrom":[subQ1,subQ0]});Q0=makeQuery(id+"F5.imprint","IMPRINT",FACE,{"disambiguationData":[TD([[makeQuery(id+"F5.imprint","IMPRINT",EDGE,{"disambiguationData":[TD([[subQ2,-1.0]])],"derivedFrom":subQ1}),-1.0]])]});}
            var Q1;
            {var subQ0=sQuery(id+"F5.wireOp",EDGE,"E34");var subQ1=sQuery(id+"F5.wireOp",EDGE,"E16");var subQ2=makeQuery(id+"F5.imprint","INTERSECT",VERTEX,{"disambiguationData":[OD(0.0)],"derivedFrom":[subQ1,subQ0]});Q1=makeQuery(id+"F5.imprint","IMPRINT",FACE,{"disambiguationData":[TD([[makeQuery(id+"F5.imprint","IMPRINT",EDGE,{"disambiguationData":[TD([[subQ2,-1.0]])],"derivedFrom":subQ1}),1.0]])]});}
            var Q2;
            {var subQ0=sQuery(id+"F5.wireOp",EDGE,"E35");var subQ1=sQuery(id+"F5.wireOp",EDGE,"E16");var subQ2=makeQuery(id+"F5.imprint","INTERSECT",VERTEX,{"disambiguationData":[OD(0.0)],"derivedFrom":[subQ1,subQ0]});Q2=makeQuery(id+"F5.imprint","IMPRINT",FACE,{"disambiguationData":[TD([[makeQuery(id+"F5.imprint","IMPRINT",EDGE,{"disambiguationData":[TD([[subQ2,-1.0]])],"derivedFrom":subQ1}),-1.0]])]});}
            var Q3;
            {var subQ0=sQuery(id+"F5.wireOp",EDGE,"E35");var subQ1=sQuery(id+"F5.wireOp",EDGE,"E16");var subQ2=makeQuery(id+"F5.imprint","INTERSECT",VERTEX,{"disambiguationData":[OD(0.0)],"derivedFrom":[subQ1,subQ0]});Q3=makeQuery(id+"F5.imprint","IMPRINT",FACE,{"disambiguationData":[TD([[makeQuery(id+"F5.imprint","IMPRINT",EDGE,{"disambiguationData":[TD([[subQ2,-1.0]])],"derivedFrom":subQ1}),1.0]])]});}
            var Q4;
            {var subQ0=sQuery(id+"F5.wireOp",EDGE,"E36");var subQ1=sQuery(id+"F5.wireOp",EDGE,"E16");var subQ2=makeQuery(id+"F5.imprint","INTERSECT",VERTEX,{"disambiguationData":[OD(0.0)],"derivedFrom":[subQ1,subQ0]});Q4=makeQuery(id+"F5.imprint","IMPRINT",FACE,{"disambiguationData":[TD([[makeQuery(id+"F5.imprint","IMPRINT",EDGE,{"disambiguationData":[TD([[subQ2,-1.0]])],"derivedFrom":subQ1}),1.0]])]});}
            var Q5;
            {var subQ0=sQuery(id+"F5.wireOp",EDGE,"E36");var subQ1=sQuery(id+"F5.wireOp",EDGE,"E16");var subQ2=makeQuery(id+"F5.imprint","INTERSECT",VERTEX,{"disambiguationData":[OD(0.0)],"derivedFrom":[subQ1,subQ0]});Q5=makeQuery(id+"F5.imprint","IMPRINT",FACE,{"disambiguationData":[TD([[makeQuery(id+"F5.imprint","IMPRINT",EDGE,{"disambiguationData":[TD([[subQ2,-1.0]])],"derivedFrom":subQ1}),-1.0]])]});}
            var Q6;
            {var subQ0=sQuery(id+"F5.wireOp",EDGE,"E37");var subQ1=sQuery(id+"F5.wireOp",EDGE,"E16");var subQ2=makeQuery(id+"F5.imprint","INTERSECT",VERTEX,{"disambiguationData":[OD(0.0)],"derivedFrom":[subQ1,subQ0]});Q6=makeQuery(id+"F5.imprint","IMPRINT",FACE,{"disambiguationData":[TD([[makeQuery(id+"F5.imprint","IMPRINT",EDGE,{"disambiguationData":[TD([[subQ2,-1.0]])],"derivedFrom":subQ1}),1.0]])]});}
            var Q7;
            {var subQ0=sQuery(id+"F5.wireOp",EDGE,"E37");var subQ1=sQuery(id+"F5.wireOp",EDGE,"E16");var subQ2=makeQuery(id+"F5.imprint","INTERSECT",VERTEX,{"disambiguationData":[OD(0.0)],"derivedFrom":[subQ1,subQ0]});Q7=makeQuery(id+"F5.imprint","IMPRINT",FACE,{"disambiguationData":[TD([[makeQuery(id+"F5.imprint","IMPRINT",EDGE,{"disambiguationData":[TD([[subQ2,-1.0]])],"derivedFrom":subQ1}),-1.0]])]});}
            var Q8;
            {var subQ1=sQuery(id+"F5.wireOp",EDGE,"E39.bottom");Q8=makeQuery(id+"F5.imprint","IMPRINT",FACE,{"disambiguationData":[TD([[makeQuery(id+"F5.imprint","IMPRINT",EDGE,{"derivedFrom":subQ1}),-1.0]])]});}
            var Q9;
            {var subQ0=sQuery(id+"F5.wireOp",EDGE,"E39.top");var subQ1=sQuery(id+"F5.wireOp",EDGE,"E16");var subQ2=makeQuery(id+"F5.imprint","INTERSECT",VERTEX,{"derivedFrom":[subQ1,subQ0]});Q9=makeQuery(id+"F5.imprint","IMPRINT",FACE,{"disambiguationData":[TD([[makeQuery(id+"F5.imprint","IMPRINT",EDGE,{"disambiguationData":[TD([[subQ2,-1.0]])],"derivedFrom":subQ1}),1.0]])]});}
            var Q10;
            {var subQ0=sQuery(id+"F5.wireOp",EDGE,"E38");var subQ1=sQuery(id+"F5.wireOp",EDGE,"E16");var subQ2=makeQuery(id+"F5.imprint","INTERSECT",VERTEX,{"disambiguationData":[OD(0.0)],"derivedFrom":[subQ1,subQ0]});Q10=makeQuery(id+"F5.imprint","IMPRINT",FACE,{"disambiguationData":[TD([[makeQuery(id+"F5.imprint","IMPRINT",EDGE,{"disambiguationData":[TD([[subQ2,-1.0]])],"derivedFrom":subQ1}),-1.0]])]});}
            var Q11;
            {var subQ0=sQuery(id+"F5.wireOp",EDGE,"E38");var subQ1=sQuery(id+"F5.wireOp",EDGE,"E16");var subQ2=makeQuery(id+"F5.imprint","INTERSECT",VERTEX,{"disambiguationData":[OD(0.0)],"derivedFrom":[subQ1,subQ0]});Q11=makeQuery(id+"F5.imprint","IMPRINT",FACE,{"disambiguationData":[TD([[makeQuery(id+"F5.imprint","IMPRINT",EDGE,{"disambiguationData":[TD([[subQ2,-1.0]])],"derivedFrom":subQ1}),1.0]])]});}
            extrude(context, id + "F9", {"entities" : qUnion([Q0, Q1, Q2, Q3, Q4, Q5, Q6, Q7, Q8, Q9, Q10, Q11]), "operationType" : NewBodyOperationType.ADD, "depth" : 11 * mm, "offsetDistance" : 25 * mm, "hasDraft" : true, "draftAngle" : 0.9 * degree, "draftPullDirection" : true});
        }
        {
            var Q0;
            Q0=makeQuery(id+"F9.opExtrude","CAP_EDGE",EDGE,{"disambiguationData":[OSD([sQuery(id+"F5.wireOp",EDGE,"E38")])],"isStart":false});
            var Q1;
            Q1=makeQuery(id+"F9.opExtrude","CAP_FACE",FACE,{"disambiguationData":[OSD([sQuery(id+"F5.wireOp",EDGE,"E34")])],"isStart":false});
            var Q2;
            Q2=makeQuery(id+"F9.opExtrude","CAP_FACE",FACE,{"disambiguationData":[OSD([sQuery(id+"F5.wireOp",EDGE,"E35")])],"isStart":false});
            var Q3;
            Q3=makeQuery(id+"F9.opExtrude","CAP_FACE",FACE,{"disambiguationData":[OSD([sQuery(id+"F5.wireOp",EDGE,"E36")])],"isStart":false});
            var Q4;
            Q4=makeQuery(id+"F9.opExtrude","CAP_FACE",FACE,{"disambiguationData":[OSD([sQuery(id+"F5.wireOp",EDGE,"E37")])],"isStart":false});
            var Q5;
            Q5=makeQuery(id+"F9.opExtrude","CAP_EDGE",EDGE,{"disambiguationData":[OSD([sQuery(id+"F5.wireOp",EDGE,"E39.left")])],"isStart":false});
            var Q6;
            Q6=makeQuery(id+"F9.opExtrude","CAP_EDGE",EDGE,{"disambiguationData":[OSD([sQuery(id+"F5.wireOp",EDGE,"E39.right")])],"isStart":false});
            var Q7;
            Q7=makeQuery(id+"F9.opExtrude","CAP_EDGE",EDGE,{"disambiguationData":[OSD([sQuery(id+"F5.wireOp",EDGE,"E39.bottom")])],"isStart":false});
            var Q8;
            Q8=makeQuery(id+"F9.opExtrude","CAP_EDGE",EDGE,{"disambiguationData":[OSD([sQuery(id+"F5.wireOp",EDGE,"E39.top")])],"isStart":false});
            fillet(context, id + "F10", {"entities" : qUnion([Q0, Q1, Q2, Q3, Q4, Q5, Q6, Q7, Q8]), "radius" : .45 * mm, "tangentPropagation" : true, "allowEdgeOverflow" : false});
        }
        {
            var Q0;
            Q0=qCreatedBy(makeId("Top.planeOp"),FACE);
            var sketch = newSketch(context, id + "F11", { "sketchPlane" : qUnion([Q0])});
            skCircle(sketch, "E40", {"center": v(0, 0) * mm, "radius": 17.33 * mm});
            skSolve(sketch);
        }
        {
            var Q0;
            Q0=makeQuery(id+"F11.imprint","IMPRINT",FACE,{"disambiguationData":[TD([[makeQuery(id+"F11.imprint","IMPRINT",EDGE,{"derivedFrom":sQuery(id+"F11.wireOp",EDGE,"E40")}),1.0]])]});
            extrude(context, id + "F12", {"entities" : qUnion([Q0]), "operationType" : NewBodyOperationType.REMOVE, "depth" : 1 * mm, "offsetDistance" : 25 * mm});
        }
        {
            var Q0;
            {var subQ0=sQuery(id+"F0.wireOp",EDGE,"E7.bottom");var subQ1=sQuery(id+"F0.wireOp",EDGE,"E1.0");Q0=makeQuery(id+"F6.boolean.opBoolean","COPY",EDGE,{"derivedFrom":makeQuery(id+"F6.opExtrude","SWEPT_EDGE",EDGE,{"disambiguationData":[OSD([subQ1,subQ0]),TDD([makeQuery(id+"F0.imprint","INTERSECT",VERTEX,{"disambiguationData":[OD(1.0)],"derivedFrom":[subQ1,subQ0]})])]})});}
            var Q1;
            {var subQ0=sQuery(id+"F0.wireOp",EDGE,"E3.left");var subQ1=sQuery(id+"F0.wireOp",EDGE,"E1.0");Q1=makeQuery(id+"F6.boolean.opBoolean","COPY",EDGE,{"derivedFrom":makeQuery(id+"F6.opExtrude","SWEPT_EDGE",EDGE,{"disambiguationData":[OSD([subQ1,subQ0]),TDD([makeQuery(id+"F0.imprint","INTERSECT",VERTEX,{"disambiguationData":[OD(0.0)],"derivedFrom":[subQ1,subQ0]})])]})});}
            var Q2;
            Q2=makeQuery(id+"F6.boolean.opBoolean","COPY",EDGE,{"derivedFrom":makeQuery(id+"F6.opExtrude","SWEPT_EDGE",EDGE,{"disambiguationData":[OSD([sQuery(id+"F0.wireOp",EDGE,"E1.0"),sQuery(id+"F0.wireOp",EDGE,"E8.left")])]})});
            var Q3;
            Q3=makeQuery(id+"F6.boolean.opBoolean","COPY",EDGE,{"derivedFrom":makeQuery(id+"F6.opExtrude","SWEPT_EDGE",EDGE,{"disambiguationData":[OSD([sQuery(id+"F0.wireOp",EDGE,"E1.0"),sQuery(id+"F0.wireOp",EDGE,"E9.left")])]})});
            var Q4;
            Q4=makeQuery(id+"F6.boolean.opBoolean","COPY",EDGE,{"derivedFrom":makeQuery(id+"F6.opExtrude","SWEPT_EDGE",EDGE,{"disambiguationData":[OSD([sQuery(id+"F0.wireOp",EDGE,"E1.0"),sQuery(id+"F0.wireOp",EDGE,"E9.right")])]})});
            var Q5;
            Q5=makeQuery(id+"F6.boolean.opBoolean","COPY",EDGE,{"derivedFrom":makeQuery(id+"F6.opExtrude","SWEPT_EDGE",EDGE,{"disambiguationData":[OSD([sQuery(id+"F0.wireOp",EDGE,"E1.0"),sQuery(id+"F0.wireOp",EDGE,"E7.top")])]})});
            var Q6;
            {var subQ0=sQuery(id+"F0.wireOp",EDGE,"E7.bottom");var subQ1=sQuery(id+"F0.wireOp",EDGE,"E1.0");Q6=makeQuery(id+"F6.boolean.opBoolean","COPY",EDGE,{"derivedFrom":makeQuery(id+"F6.opExtrude","SWEPT_EDGE",EDGE,{"disambiguationData":[OSD([subQ1,subQ0]),TDD([makeQuery(id+"F0.imprint","INTERSECT",VERTEX,{"disambiguationData":[OD(0.0)],"derivedFrom":[subQ1,subQ0]})])]})});}
            var Q7;
            {var subQ0=sQuery(id+"F0.wireOp",EDGE,"E6.top");var subQ1=sQuery(id+"F0.wireOp",EDGE,"E1.0");Q7=makeQuery(id+"F6.boolean.opBoolean","COPY",EDGE,{"derivedFrom":makeQuery(id+"F6.opExtrude","SWEPT_EDGE",EDGE,{"disambiguationData":[OSD([subQ1,subQ0]),TDD([makeQuery(id+"F0.imprint","INTERSECT",VERTEX,{"disambiguationData":[OD(0.0)],"derivedFrom":[subQ1,subQ0]})])]})});}
            var Q8;
            Q8=makeQuery(id+"F6.boolean.opBoolean","COPY",EDGE,{"derivedFrom":makeQuery(id+"F6.opExtrude","SWEPT_EDGE",EDGE,{"disambiguationData":[OSD([sQuery(id+"F0.wireOp",EDGE,"E1.0"),sQuery(id+"F0.wireOp",EDGE,"E6.bottom")])]})});
            var Q9;
            Q9=makeQuery(id+"F6.boolean.opBoolean","COPY",EDGE,{"derivedFrom":makeQuery(id+"F6.opExtrude","SWEPT_EDGE",EDGE,{"disambiguationData":[OSD([sQuery(id+"F0.wireOp",EDGE,"E1.0"),sQuery(id+"F0.wireOp",EDGE,"E3.right")])]})});
            var Q10;
            {var subQ0=sQuery(id+"F0.wireOp",EDGE,"E3.left");var subQ1=sQuery(id+"F0.wireOp",EDGE,"E1.0");Q10=makeQuery(id+"F6.boolean.opBoolean","COPY",EDGE,{"derivedFrom":makeQuery(id+"F6.opExtrude","SWEPT_EDGE",EDGE,{"disambiguationData":[OSD([subQ1,subQ0]),TDD([makeQuery(id+"F0.imprint","INTERSECT",VERTEX,{"disambiguationData":[OD(1.0)],"derivedFrom":[subQ1,subQ0]})])]})});}
            var Q11;
            Q11=makeQuery(id+"F6.boolean.opBoolean","COPY",EDGE,{"derivedFrom":makeQuery(id+"F6.opExtrude","SWEPT_EDGE",EDGE,{"disambiguationData":[OSD([sQuery(id+"F0.wireOp",EDGE,"E1.0"),sQuery(id+"F0.wireOp",EDGE,"E2.left")])]})});
            var Q12;
            {var subQ0=sQuery(id+"F0.wireOp",EDGE,"E6.top");var subQ1=sQuery(id+"F0.wireOp",EDGE,"E1.0");Q12=makeQuery(id+"F6.boolean.opBoolean","COPY",EDGE,{"derivedFrom":makeQuery(id+"F6.opExtrude","SWEPT_EDGE",EDGE,{"disambiguationData":[OSD([subQ1,subQ0]),TDD([makeQuery(id+"F0.imprint","INTERSECT",VERTEX,{"disambiguationData":[OD(1.0)],"derivedFrom":[subQ1,subQ0]})])]})});}
            var Q13;
            Q13=makeQuery(id+"F6.boolean.opBoolean","COPY",EDGE,{"derivedFrom":makeQuery(id+"F6.opExtrude","SWEPT_EDGE",EDGE,{"disambiguationData":[OSD([sQuery(id+"F0.wireOp",EDGE,"E1.0"),sQuery(id+"F0.wireOp",EDGE,"E2.right")])]})});
            fillet(context, id + "F13", {"entities" : qUnion([Q0, Q1, Q2, Q3, Q4, Q5, Q6, Q7, Q8, Q9, Q10, Q11, Q12, Q13]), "radius" : 1 * mm, "tangentPropagation" : true, "allowEdgeOverflow" : false});
        }
        {
            var Q0;
            {var subQ0=sQuery(id+"F0.wireOp",EDGE,"E11");var subQ1=sQuery(id+"F0.wireOp",EDGE,"E8.right");var subQ2=makeQuery(id+"F0.imprint","INTERSECT",VERTEX,{"disambiguationData":[OD(1.0)],"derivedFrom":[subQ1,subQ0]});Q0=makeQuery(id+"F0.imprint","IMPRINT",FACE,{"disambiguationData":[TD([[makeQuery(id+"F0.imprint","IMPRINT",EDGE,{"disambiguationData":[TD([[subQ2,-1.0]])],"derivedFrom":subQ1}),1.0]])]});}
            var Q1;
            {var subQ0=sQuery(id+"F0.wireOp",EDGE,"E11");var subQ1=sQuery(id+"F0.wireOp",EDGE,"E9.left");var subQ2=makeQuery(id+"F0.imprint","INTERSECT",VERTEX,{"disambiguationData":[OD(1.0)],"derivedFrom":[subQ1,subQ0]});Q1=makeQuery(id+"F0.imprint","IMPRINT",FACE,{"disambiguationData":[TD([[makeQuery(id+"F0.imprint","IMPRINT",EDGE,{"disambiguationData":[TD([[subQ2,-1.0]])],"derivedFrom":subQ1}),1.0]])]});}
            var Q2;
            {var subQ0=sQuery(id+"F0.wireOp",EDGE,"E11");var subQ1=sQuery(id+"F0.wireOp",EDGE,"E8.left");var subQ2=makeQuery(id+"F0.imprint","INTERSECT",VERTEX,{"disambiguationData":[OD(1.0)],"derivedFrom":[subQ1,subQ0]});Q2=makeQuery(id+"F0.imprint","IMPRINT",FACE,{"disambiguationData":[TD([[makeQuery(id+"F0.imprint","IMPRINT",EDGE,{"disambiguationData":[TD([[subQ2,-1.0]])],"derivedFrom":subQ1}),1.0]])]});}
            var Q3;
            {var subQ0=sQuery(id+"F0.wireOp",EDGE,"E11");var subQ5=sQuery(id+"F0.wireOp",EDGE,"E9.right");var subQ6=makeQuery(id+"F0.imprint","INTERSECT",VERTEX,{"disambiguationData":[OD(1.0)],"derivedFrom":[subQ5,subQ0]});Q3=makeQuery(id+"F0.imprint","IMPRINT",FACE,{"disambiguationData":[TD([[makeQuery(id+"F0.imprint","IMPRINT",EDGE,{"disambiguationData":[TD([[subQ6,-1.0]])],"derivedFrom":subQ5}),1.0]])]});}
            var Q4;
            {var subQ0=sQuery(id+"F0.wireOp",EDGE,"E11");var subQ5=sQuery(id+"F0.wireOp",EDGE,"E8.left");var subQ6=makeQuery(id+"F0.imprint","INTERSECT",VERTEX,{"disambiguationData":[OD(1.0)],"derivedFrom":[subQ5,subQ0]});Q4=makeQuery(id+"F0.imprint","IMPRINT",FACE,{"disambiguationData":[TD([[makeQuery(id+"F0.imprint","IMPRINT",EDGE,{"disambiguationData":[TD([[subQ6,-1.0]])],"derivedFrom":subQ5}),-1.0]])]});}
            var Q5;
            {var subQ0=sQuery(id+"F0.wireOp",EDGE,"E12");Q5=makeQuery(id+"F0.imprint","IMPRINT",FACE,{"disambiguationData":[TD([[makeQuery(id+"F0.imprint","IMPRINT",EDGE,{"derivedFrom":subQ0}),-1.0]])]});}
            var Q6;
            {var subQ0=sQuery(id+"F0.wireOp",EDGE,"E13");Q6=makeQuery(id+"F0.imprint","IMPRINT",FACE,{"disambiguationData":[TD([[makeQuery(id+"F0.imprint","IMPRINT",EDGE,{"derivedFrom":subQ0}),-1.0]])]});}
            extrude(context, id + "F14", {"entities" : qUnion([Q0, Q1, Q2, Q3, Q4, Q5, Q6]), "operationType" : NewBodyOperationType.ADD, "depth" : 1 * mm, "offsetDistance" : 25 * mm});
        }
        {
            var Q0;
            {var subQ0=sQuery(id+"F5.wireOp",EDGE,"E38");var subQ1=sQuery(id+"F5.wireOp",EDGE,"E16");var subQ2=makeQuery(id+"F5.imprint","INTERSECT",VERTEX,{"disambiguationData":[OD(0.0)],"derivedFrom":[subQ1,subQ0]});Q0=makeQuery(id+"F5.imprint","IMPRINT",FACE,{"disambiguationData":[TD([[makeQuery(id+"F5.imprint","IMPRINT",EDGE,{"disambiguationData":[TD([[subQ2,-1.0]])],"derivedFrom":subQ1}),-1.0]])]});}
            var Q1;
            {var subQ0=sQuery(id+"F5.wireOp",EDGE,"E38");var subQ1=sQuery(id+"F5.wireOp",EDGE,"E16");var subQ2=makeQuery(id+"F5.imprint","INTERSECT",VERTEX,{"disambiguationData":[OD(0.0)],"derivedFrom":[subQ1,subQ0]});Q1=makeQuery(id+"F5.imprint","IMPRINT",FACE,{"disambiguationData":[TD([[makeQuery(id+"F5.imprint","IMPRINT",EDGE,{"disambiguationData":[TD([[subQ2,-1.0]])],"derivedFrom":subQ1}),1.0]])]});}
            var Q2;
            {var subQ1=sQuery(id+"F5.wireOp",EDGE,"E39.bottom");Q2=makeQuery(id+"F5.imprint","IMPRINT",FACE,{"disambiguationData":[TD([[makeQuery(id+"F5.imprint","IMPRINT",EDGE,{"derivedFrom":subQ1}),-1.0]])]});}
            var Q3;
            {var subQ0=sQuery(id+"F5.wireOp",EDGE,"E39.top");var subQ1=sQuery(id+"F5.wireOp",EDGE,"E16");var subQ2=makeQuery(id+"F5.imprint","INTERSECT",VERTEX,{"derivedFrom":[subQ1,subQ0]});Q3=makeQuery(id+"F5.imprint","IMPRINT",FACE,{"disambiguationData":[TD([[makeQuery(id+"F5.imprint","IMPRINT",EDGE,{"disambiguationData":[TD([[subQ2,-1.0]])],"derivedFrom":subQ1}),1.0]])]});}
            var Q4;
            {var subQ0=sQuery(id+"F5.wireOp",EDGE,"E37");var subQ1=sQuery(id+"F5.wireOp",EDGE,"E16");var subQ2=makeQuery(id+"F5.imprint","INTERSECT",VERTEX,{"disambiguationData":[OD(0.0)],"derivedFrom":[subQ1,subQ0]});Q4=makeQuery(id+"F5.imprint","IMPRINT",FACE,{"disambiguationData":[TD([[makeQuery(id+"F5.imprint","IMPRINT",EDGE,{"disambiguationData":[TD([[subQ2,-1.0]])],"derivedFrom":subQ1}),1.0]])]});}
            var Q5;
            {var subQ0=sQuery(id+"F5.wireOp",EDGE,"E37");var subQ1=sQuery(id+"F5.wireOp",EDGE,"E16");var subQ2=makeQuery(id+"F5.imprint","INTERSECT",VERTEX,{"disambiguationData":[OD(0.0)],"derivedFrom":[subQ1,subQ0]});Q5=makeQuery(id+"F5.imprint","IMPRINT",FACE,{"disambiguationData":[TD([[makeQuery(id+"F5.imprint","IMPRINT",EDGE,{"disambiguationData":[TD([[subQ2,-1.0]])],"derivedFrom":subQ1}),-1.0]])]});}
            var Q6;
            {var subQ0=sQuery(id+"F5.wireOp",EDGE,"E36");var subQ1=sQuery(id+"F5.wireOp",EDGE,"E16");var subQ2=makeQuery(id+"F5.imprint","INTERSECT",VERTEX,{"disambiguationData":[OD(0.0)],"derivedFrom":[subQ1,subQ0]});Q6=makeQuery(id+"F5.imprint","IMPRINT",FACE,{"disambiguationData":[TD([[makeQuery(id+"F5.imprint","IMPRINT",EDGE,{"disambiguationData":[TD([[subQ2,-1.0]])],"derivedFrom":subQ1}),1.0]])]});}
            var Q7;
            {var subQ0=sQuery(id+"F5.wireOp",EDGE,"E36");var subQ1=sQuery(id+"F5.wireOp",EDGE,"E16");var subQ2=makeQuery(id+"F5.imprint","INTERSECT",VERTEX,{"disambiguationData":[OD(0.0)],"derivedFrom":[subQ1,subQ0]});Q7=makeQuery(id+"F5.imprint","IMPRINT",FACE,{"disambiguationData":[TD([[makeQuery(id+"F5.imprint","IMPRINT",EDGE,{"disambiguationData":[TD([[subQ2,-1.0]])],"derivedFrom":subQ1}),-1.0]])]});}
            var Q8;
            {var subQ0=sQuery(id+"F5.wireOp",EDGE,"E35");var subQ1=sQuery(id+"F5.wireOp",EDGE,"E16");var subQ2=makeQuery(id+"F5.imprint","INTERSECT",VERTEX,{"disambiguationData":[OD(0.0)],"derivedFrom":[subQ1,subQ0]});Q8=makeQuery(id+"F5.imprint","IMPRINT",FACE,{"disambiguationData":[TD([[makeQuery(id+"F5.imprint","IMPRINT",EDGE,{"disambiguationData":[TD([[subQ2,-1.0]])],"derivedFrom":subQ1}),1.0]])]});}
            var Q9;
            {var subQ0=sQuery(id+"F5.wireOp",EDGE,"E35");var subQ1=sQuery(id+"F5.wireOp",EDGE,"E16");var subQ2=makeQuery(id+"F5.imprint","INTERSECT",VERTEX,{"disambiguationData":[OD(0.0)],"derivedFrom":[subQ1,subQ0]});Q9=makeQuery(id+"F5.imprint","IMPRINT",FACE,{"disambiguationData":[TD([[makeQuery(id+"F5.imprint","IMPRINT",EDGE,{"disambiguationData":[TD([[subQ2,-1.0]])],"derivedFrom":subQ1}),-1.0]])]});}
            var Q10;
            {var subQ0=sQuery(id+"F5.wireOp",EDGE,"E34");var subQ1=sQuery(id+"F5.wireOp",EDGE,"E16");var subQ2=makeQuery(id+"F5.imprint","INTERSECT",VERTEX,{"disambiguationData":[OD(0.0)],"derivedFrom":[subQ1,subQ0]});Q10=makeQuery(id+"F5.imprint","IMPRINT",FACE,{"disambiguationData":[TD([[makeQuery(id+"F5.imprint","IMPRINT",EDGE,{"disambiguationData":[TD([[subQ2,-1.0]])],"derivedFrom":subQ1}),-1.0]])]});}
            var Q11;
            {var subQ0=sQuery(id+"F5.wireOp",EDGE,"E34");var subQ1=sQuery(id+"F5.wireOp",EDGE,"E16");var subQ2=makeQuery(id+"F5.imprint","INTERSECT",VERTEX,{"disambiguationData":[OD(0.0)],"derivedFrom":[subQ1,subQ0]});Q11=makeQuery(id+"F5.imprint","IMPRINT",FACE,{"disambiguationData":[TD([[makeQuery(id+"F5.imprint","IMPRINT",EDGE,{"disambiguationData":[TD([[subQ2,-1.0]])],"derivedFrom":subQ1}),1.0]])]});}
            extrude(context, id + "F15", {"entities" : qUnion([Q0, Q1, Q2, Q3, Q4, Q5, Q6, Q7, Q8, Q9, Q10, Q11]), "operationType" : NewBodyOperationType.REMOVE, "depth" : 3 * mm, "offsetDistance" : 25 * mm});
        }
    });
